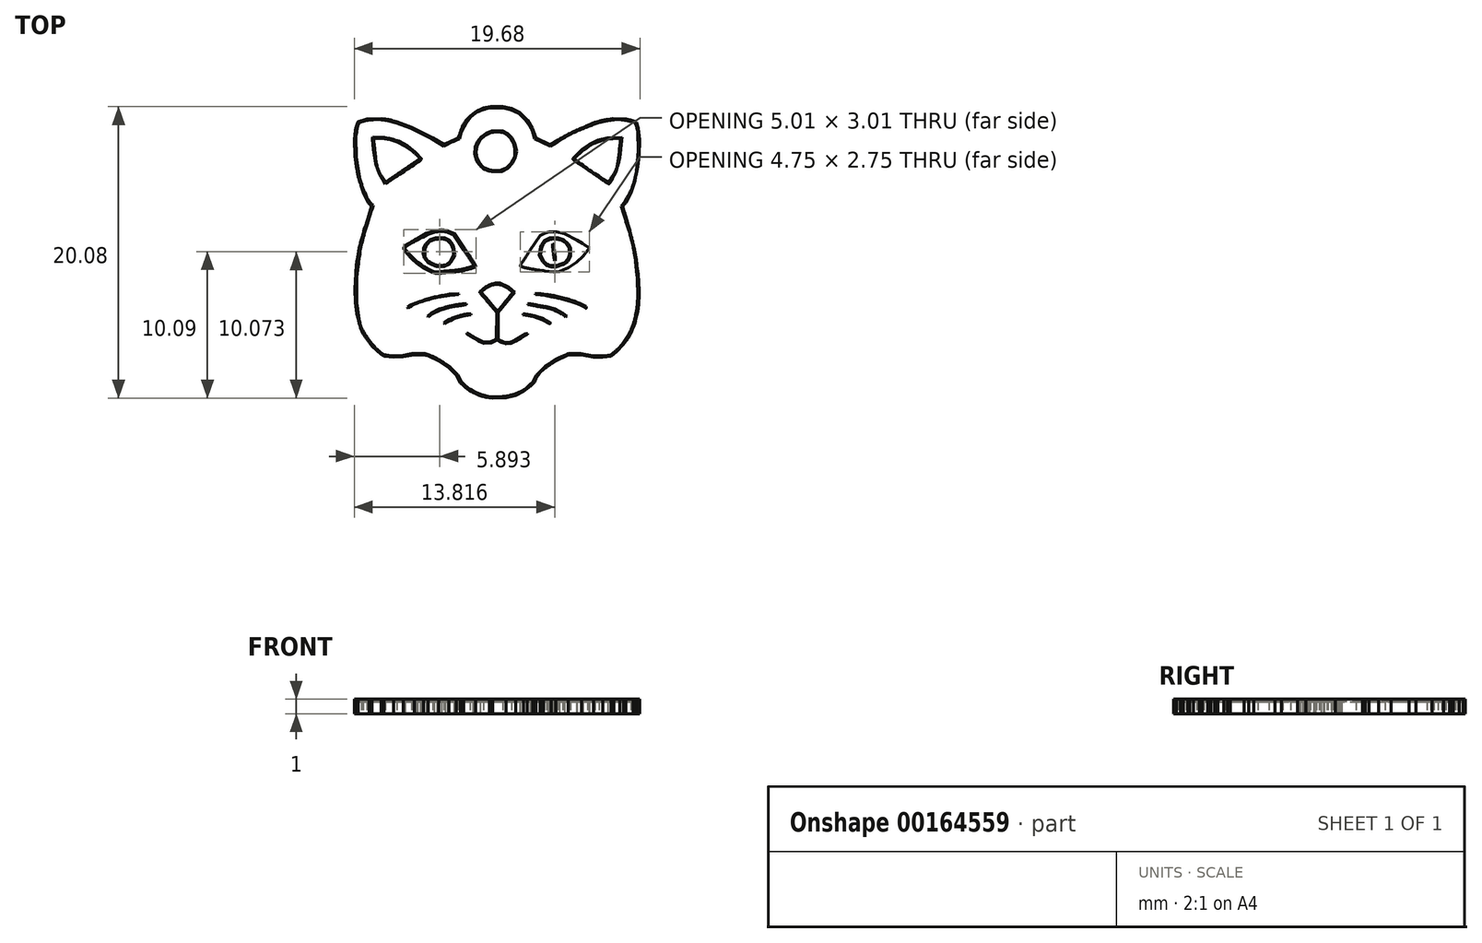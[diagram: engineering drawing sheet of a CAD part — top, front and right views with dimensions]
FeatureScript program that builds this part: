
annotation { "Feature Type Name" : "Feature", "Feature Type Description" : "" }
export const myFeature = defineFeature(function(context is Context, id is Id, definition is map)
    precondition{}
    {
        {
            var Q0;
            Q0=qCreatedBy(makeId("Top.planeOp"),FACE);
            var sketch = newSketch(context, id + "F0", { "sketchPlane" : qUnion([Q0])});
            skFitSpline(sketch, "E0", {"points": [v(-0.53, -10.01) * mm, v(-0.8, -9.97) * mm, v(-1.27, -9.84) * mm, v(-1.49, -9.74) * mm]});
            skFitSpline(sketch, "E1", {"points": [v(-1.49, -9.74) * mm, v(-1.72, -9.63) * mm, v(-2.05, -9.42) * mm, v(-2.3, -9.2) * mm]});
            skLineSegment(sketch, "E2", {"start": v(-2.3, -9.2) * mm, "end": v(-2.52, -9.01) * mm});
            skLineSegment(sketch, "E3", {"start": v(-2.52, -9.01) * mm, "end": v(-2.66, -8.74) * mm});
            skLineSegment(sketch, "E4", {"start": v(-2.66, -8.74) * mm, "end": v(-2.8, -8.47) * mm});
            skLineSegment(sketch, "E5", {"start": v(-2.8, -8.47) * mm, "end": v(-3.06, -8.22) * mm});
            skLineSegment(sketch, "E6", {"start": v(-3.06, -8.22) * mm, "end": v(-3.31, -7.96) * mm});
            skLineSegment(sketch, "E7", {"start": v(-3.31, -7.96) * mm, "end": v(-3.67, -7.72) * mm});
            skLineSegment(sketch, "E8", {"start": v(-3.67, -7.72) * mm, "end": v(-4.03, -7.49) * mm});
            skLineSegment(sketch, "E9", {"start": v(-4.03, -7.49) * mm, "end": v(-4.4, -7.3) * mm});
            skLineSegment(sketch, "E10", {"start": v(-4.4, -7.3) * mm, "end": v(-4.76, -7.13) * mm});
            skLineSegment(sketch, "E11", {"start": v(-4.76, -7.13) * mm, "end": v(-4.91, -7.1) * mm});
            skLineSegment(sketch, "E12", {"start": v(-4.91, -7.1) * mm, "end": v(-5.06, -7.06) * mm});
            skLineSegment(sketch, "E13", {"start": v(-5.06, -7.06) * mm, "end": v(-5.38, -7.06) * mm});
            skLineSegment(sketch, "E14", {"start": v(-5.38, -7.06) * mm, "end": v(-5.7, -7.06) * mm});
            skLineSegment(sketch, "E15", {"start": v(-5.7, -7.06) * mm, "end": v(-6.08, -7.12) * mm});
            skLineSegment(sketch, "E16", {"start": v(-6.08, -7.12) * mm, "end": v(-6.46, -7.2) * mm});
            skLineSegment(sketch, "E17", {"start": v(-6.46, -7.2) * mm, "end": v(-6.8, -7.21) * mm});
            skLineSegment(sketch, "E18", {"start": v(-6.8, -7.21) * mm, "end": v(-7.13, -7.23) * mm});
            skLineSegment(sketch, "E19", {"start": v(-7.13, -7.23) * mm, "end": v(-7.46, -7.2) * mm});
            skLineSegment(sketch, "E20", {"start": v(-7.46, -7.2) * mm, "end": v(-7.79, -7.15) * mm});
            skLineSegment(sketch, "E21", {"start": v(-7.79, -7.15) * mm, "end": v(-7.9, -7.1) * mm});
            skLineSegment(sketch, "E22", {"start": v(-7.9, -7.1) * mm, "end": v(-8, -7.05) * mm});
            skLineSegment(sketch, "E23", {"start": v(-8, -7.05) * mm, "end": v(-8.3, -6.76) * mm});
            skLineSegment(sketch, "E24", {"start": v(-8.3, -6.76) * mm, "end": v(-8.61, -6.48) * mm});
            skLineSegment(sketch, "E25", {"start": v(-8.61, -6.48) * mm, "end": v(-8.8, -6.22) * mm});
            skFitSpline(sketch, "E26", {"points": [v(-8.8, -6.22) * mm, v(-9.16, -5.74) * mm, v(-9.4, -5.2) * mm, v(-9.58, -4.56) * mm]});
            skLineSegment(sketch, "E27", {"start": v(-9.58, -4.56) * mm, "end": v(-9.66, -4.24) * mm});
            skLineSegment(sketch, "E28", {"start": v(-9.66, -4.24) * mm, "end": v(-9.71, -3.86) * mm});
            skLineSegment(sketch, "E29", {"start": v(-9.71, -3.86) * mm, "end": v(-9.76, -3.49) * mm});
            skLineSegment(sketch, "E30", {"start": v(-9.76, -3.49) * mm, "end": v(-9.78, -3) * mm});
            skLineSegment(sketch, "E31", {"start": v(-9.78, -3) * mm, "end": v(-9.8, -2.53) * mm});
            skLineSegment(sketch, "E32", {"start": v(-9.8, -2.53) * mm, "end": v(-9.76, -1.98) * mm});
            skFitSpline(sketch, "E33", {"points": [v(-9.76, -1.98) * mm, v(-9.67, -0.63) * mm, v(-9.37, 0.83) * mm, v(-8.85, 2.51) * mm]});
            skLineSegment(sketch, "E34", {"start": v(-8.85, 2.51) * mm, "end": v(-8.64, 3.2) * mm});
            skLineSegment(sketch, "E35", {"start": v(-8.64, 3.2) * mm, "end": v(-8.76, 3.3) * mm});
            skLineSegment(sketch, "E36", {"start": v(-8.76, 3.3) * mm, "end": v(-8.87, 3.42) * mm});
            skLineSegment(sketch, "E37", {"start": v(-8.87, 3.42) * mm, "end": v(-9.05, 3.77) * mm});
            skLineSegment(sketch, "E38", {"start": v(-9.05, 3.77) * mm, "end": v(-9.22, 4.13) * mm});
            skLineSegment(sketch, "E39", {"start": v(-9.22, 4.13) * mm, "end": v(-9.36, 4.54) * mm});
            skFitSpline(sketch, "E40", {"points": [v(-9.36, 4.54) * mm, v(-9.51, 5.02) * mm, v(-9.64, 5.58) * mm, v(-9.73, 6.17) * mm]});
            skLineSegment(sketch, "E41", {"start": v(-9.73, 6.17) * mm, "end": v(-9.8, 6.6) * mm});
            skLineSegment(sketch, "E42", {"start": v(-9.8, 6.6) * mm, "end": v(-9.82, 7.19) * mm});
            skLineSegment(sketch, "E43", {"start": v(-9.82, 7.19) * mm, "end": v(-9.84, 7.77) * mm});
            skLineSegment(sketch, "E44", {"start": v(-9.84, 7.77) * mm, "end": v(-9.8, 8.1) * mm});
            skLineSegment(sketch, "E45", {"start": v(-9.8, 8.1) * mm, "end": v(-9.76, 8.43) * mm});
            skLineSegment(sketch, "E46", {"start": v(-9.76, 8.43) * mm, "end": v(-9.7, 8.68) * mm});
            skFitSpline(sketch, "E47", {"points": [v(-9.7, 8.68) * mm, v(-9.65, 8.82) * mm, v(-9.61, 8.95) * mm, v(-9.6, 8.97) * mm]});
            skLineSegment(sketch, "E48", {"start": v(-9.6, 8.97) * mm, "end": v(-9.58, 9) * mm});
            skLineSegment(sketch, "E49", {"start": v(-9.58, 9) * mm, "end": v(-9.28, 9.1) * mm});
            skLineSegment(sketch, "E50", {"start": v(-9.28, 9.1) * mm, "end": v(-8.98, 9.19) * mm});
            skLineSegment(sketch, "E51", {"start": v(-8.98, 9.19) * mm, "end": v(-8.48, 9.2) * mm});
            skLineSegment(sketch, "E52", {"start": v(-8.48, 9.2) * mm, "end": v(-7.97, 9.22) * mm});
            skLineSegment(sketch, "E53", {"start": v(-7.97, 9.22) * mm, "end": v(-7.7, 9.18) * mm});
            skFitSpline(sketch, "E54", {"points": [v(-7.7, 9.18) * mm, v(-7.54, 9.16) * mm, v(-7.3, 9.11) * mm, v(-7.16, 9.08) * mm]});
            skLineSegment(sketch, "E55", {"start": v(-7.16, 9.08) * mm, "end": v(-6.91, 9.01) * mm});
            skLineSegment(sketch, "E56", {"start": v(-6.91, 9.01) * mm, "end": v(-6.4, 8.81) * mm});
            skLineSegment(sketch, "E57", {"start": v(-6.4, 8.81) * mm, "end": v(-5.9, 8.6) * mm});
            skLineSegment(sketch, "E58", {"start": v(-5.9, 8.6) * mm, "end": v(-5.16, 8.25) * mm});
            skLineSegment(sketch, "E59", {"start": v(-5.16, 8.25) * mm, "end": v(-4.43, 7.89) * mm});
            skLineSegment(sketch, "E60", {"start": v(-4.43, 7.89) * mm, "end": v(-4.05, 7.66) * mm});
            skLineSegment(sketch, "E61", {"start": v(-4.05, 7.66) * mm, "end": v(-3.67, 7.43) * mm});
            skLineSegment(sketch, "E62", {"start": v(-3.67, 7.43) * mm, "end": v(-3.44, 7.53) * mm});
            skFitSpline(sketch, "E63", {"points": [v(-3.44, 7.53) * mm, v(-3.3, 7.6) * mm, v(-3.08, 7.7) * mm, v(-2.94, 7.77) * mm]});
            skLineSegment(sketch, "E64", {"start": v(-2.94, 7.77) * mm, "end": v(-2.68, 7.9) * mm});
            skLineSegment(sketch, "E65", {"start": v(-2.68, 7.9) * mm, "end": v(-2.57, 8.18) * mm});
            skFitSpline(sketch, "E66", {"points": [v(-2.57, 8.18) * mm, v(-2.38, 8.7) * mm, v(-2.16, 9.07) * mm, v(-1.85, 9.37) * mm]});
            skLineSegment(sketch, "E67", {"start": v(-1.85, 9.37) * mm, "end": v(-1.68, 9.55) * mm});
            skLineSegment(sketch, "E68", {"start": v(-1.68, 9.55) * mm, "end": v(-1.5, 9.66) * mm});
            skFitSpline(sketch, "E69", {"points": [v(-1.5, 9.66) * mm, v(-1.42, 9.72) * mm, v(-1.25, 9.8) * mm, v(-1.14, 9.85) * mm]});
            skLineSegment(sketch, "E70", {"start": v(-1.14, 9.85) * mm, "end": v(-0.95, 9.94) * mm});
            skLineSegment(sketch, "E71", {"start": v(-0.95, 9.94) * mm, "end": v(-0.69, 9.99) * mm});
            skLineSegment(sketch, "E72", {"start": v(-0.69, 9.99) * mm, "end": v(-0.43, 10.04) * mm});
            skLineSegment(sketch, "E73", {"start": v(-0.43, 10.04) * mm, "end": v(-0.03, 10.04) * mm});
            skLineSegment(sketch, "E74", {"start": v(-0.03, 10.04) * mm, "end": v(0.38, 10.04) * mm});
            skLineSegment(sketch, "E75", {"start": v(0.38, 10.04) * mm, "end": v(0.7, 9.98) * mm});
            skLineSegment(sketch, "E76", {"start": v(0.7, 9.98) * mm, "end": v(1, 9.91) * mm});
            skLineSegment(sketch, "E77", {"start": v(1, 9.91) * mm, "end": v(1.29, 9.77) * mm});
            skLineSegment(sketch, "E78", {"start": v(1.29, 9.77) * mm, "end": v(1.57, 9.64) * mm});
            skLineSegment(sketch, "E79", {"start": v(1.57, 9.64) * mm, "end": v(1.84, 9.36) * mm});
            skLineSegment(sketch, "E80", {"start": v(1.84, 9.36) * mm, "end": v(2.1, 9.1) * mm});
            skLineSegment(sketch, "E81", {"start": v(2.1, 9.1) * mm, "end": v(2.27, 8.83) * mm});
            skLineSegment(sketch, "E82", {"start": v(2.27, 8.83) * mm, "end": v(2.42, 8.56) * mm});
            skLineSegment(sketch, "E83", {"start": v(2.42, 8.56) * mm, "end": v(2.55, 8.22) * mm});
            skLineSegment(sketch, "E84", {"start": v(2.55, 8.22) * mm, "end": v(2.68, 7.88) * mm});
            skLineSegment(sketch, "E85", {"start": v(2.68, 7.88) * mm, "end": v(3.17, 7.65) * mm});
            skLineSegment(sketch, "E86", {"start": v(3.17, 7.65) * mm, "end": v(3.66, 7.42) * mm});
            skLineSegment(sketch, "E87", {"start": v(3.66, 7.42) * mm, "end": v(4.08, 7.67) * mm});
            skFitSpline(sketch, "E88", {"points": [v(4.08, 7.67) * mm, v(4.62, 8) * mm, v(5.55, 8.45) * mm, v(6.23, 8.73) * mm]});
            skLineSegment(sketch, "E89", {"start": v(6.23, 8.73) * mm, "end": v(6.76, 8.95) * mm});
            skLineSegment(sketch, "E90", {"start": v(6.76, 8.95) * mm, "end": v(7.04, 9.03) * mm});
            skFitSpline(sketch, "E91", {"points": [v(7.04, 9.03) * mm, v(7.2, 9.08) * mm, v(7.47, 9.14) * mm, v(7.65, 9.17) * mm]});
            skLineSegment(sketch, "E92", {"start": v(7.65, 9.17) * mm, "end": v(7.98, 9.22) * mm});
            skLineSegment(sketch, "E93", {"start": v(7.98, 9.22) * mm, "end": v(8.45, 9.2) * mm});
            skLineSegment(sketch, "E94", {"start": v(8.45, 9.2) * mm, "end": v(8.92, 9.19) * mm});
            skLineSegment(sketch, "E95", {"start": v(8.92, 9.19) * mm, "end": v(9.17, 9.12) * mm});
            skFitSpline(sketch, "E96", {"points": [v(9.17, 9.12) * mm, v(9.32, 9.08) * mm, v(9.47, 9.03) * mm, v(9.52, 9) * mm]});
            skLineSegment(sketch, "E97", {"start": v(9.52, 9) * mm, "end": v(9.6, 8.96) * mm});
            skLineSegment(sketch, "E98", {"start": v(9.6, 8.96) * mm, "end": v(9.67, 8.76) * mm});
            skLineSegment(sketch, "E99", {"start": v(9.67, 8.76) * mm, "end": v(9.73, 8.56) * mm});
            skLineSegment(sketch, "E100", {"start": v(9.73, 8.56) * mm, "end": v(9.78, 8.17) * mm});
            skLineSegment(sketch, "E101", {"start": v(9.78, 8.17) * mm, "end": v(9.84, 7.77) * mm});
            skLineSegment(sketch, "E102", {"start": v(9.84, 7.77) * mm, "end": v(9.82, 7.2) * mm});
            skLineSegment(sketch, "E103", {"start": v(9.82, 7.2) * mm, "end": v(9.8, 6.64) * mm});
            skLineSegment(sketch, "E104", {"start": v(9.8, 6.64) * mm, "end": v(9.73, 6.17) * mm});
            skFitSpline(sketch, "E105", {"points": [v(9.73, 6.17) * mm, v(9.7, 5.92) * mm, v(9.62, 5.54) * mm, v(9.58, 5.33) * mm]});
            skLineSegment(sketch, "E106", {"start": v(9.58, 5.33) * mm, "end": v(9.5, 4.95) * mm});
            skLineSegment(sketch, "E107", {"start": v(9.5, 4.95) * mm, "end": v(9.35, 4.5) * mm});
            skLineSegment(sketch, "E108", {"start": v(9.35, 4.5) * mm, "end": v(9.2, 4.07) * mm});
            skLineSegment(sketch, "E109", {"start": v(9.2, 4.07) * mm, "end": v(9.03, 3.74) * mm});
            skLineSegment(sketch, "E110", {"start": v(9.03, 3.74) * mm, "end": v(8.87, 3.42) * mm});
            skLineSegment(sketch, "E111", {"start": v(8.87, 3.42) * mm, "end": v(8.75, 3.3) * mm});
            skLineSegment(sketch, "E112", {"start": v(8.75, 3.3) * mm, "end": v(8.63, 3.17) * mm});
            skLineSegment(sketch, "E113", {"start": v(8.63, 3.17) * mm, "end": v(8.7, 2.98) * mm});
            skFitSpline(sketch, "E114", {"points": [v(8.7, 2.98) * mm, v(8.81, 2.66) * mm, v(9.12, 1.6) * mm, v(9.24, 1.1) * mm]});
            skFitSpline(sketch, "E115", {"points": [v(9.24, 1.1) * mm, v(9.42, 0.4) * mm, v(9.55, -0.28) * mm, v(9.64, -0.92) * mm]});
            skLineSegment(sketch, "E116", {"start": v(9.64, -0.92) * mm, "end": v(9.73, -1.5) * mm});
            skLineSegment(sketch, "E117", {"start": v(9.73, -1.5) * mm, "end": v(9.76, -2.06) * mm});
            skLineSegment(sketch, "E118", {"start": v(9.76, -2.06) * mm, "end": v(9.8, -2.63) * mm});
            skLineSegment(sketch, "E119", {"start": v(9.8, -2.63) * mm, "end": v(9.78, -3.06) * mm});
            skFitSpline(sketch, "E120", {"points": [v(9.78, -3.06) * mm, v(9.75, -3.6) * mm, v(9.69, -4.09) * mm, v(9.58, -4.53) * mm]});
            skLineSegment(sketch, "E121", {"start": v(9.58, -4.53) * mm, "end": v(9.5, -4.88) * mm});
            skLineSegment(sketch, "E122", {"start": v(9.5, -4.88) * mm, "end": v(9.38, -5.18) * mm});
            skFitSpline(sketch, "E123", {"points": [v(9.38, -5.18) * mm, v(9.23, -5.54) * mm, v(9.08, -5.83) * mm, v(8.87, -6.13) * mm]});
            skLineSegment(sketch, "E124", {"start": v(8.87, -6.13) * mm, "end": v(8.72, -6.34) * mm});
            skLineSegment(sketch, "E125", {"start": v(8.72, -6.34) * mm, "end": v(8.47, -6.6) * mm});
            skFitSpline(sketch, "E126", {"points": [v(8.47, -6.6) * mm, v(8.33, -6.75) * mm, v(8.14, -6.93) * mm, v(8.04, -7) * mm]});
            skLineSegment(sketch, "E127", {"start": v(8.04, -7) * mm, "end": v(7.85, -7.15) * mm});
            skLineSegment(sketch, "E128", {"start": v(7.85, -7.15) * mm, "end": v(7.57, -7.19) * mm});
            skLineSegment(sketch, "E129", {"start": v(7.57, -7.19) * mm, "end": v(7.3, -7.22) * mm});
            skLineSegment(sketch, "E130", {"start": v(7.3, -7.22) * mm, "end": v(6.98, -7.22) * mm});
            skLineSegment(sketch, "E131", {"start": v(6.98, -7.22) * mm, "end": v(6.66, -7.22) * mm});
            skLineSegment(sketch, "E132", {"start": v(6.66, -7.22) * mm, "end": v(6.24, -7.15) * mm});
            skLineSegment(sketch, "E133", {"start": v(6.24, -7.15) * mm, "end": v(5.83, -7.08) * mm});
            skLineSegment(sketch, "E134", {"start": v(5.83, -7.08) * mm, "end": v(5.36, -7.08) * mm});
            skLineSegment(sketch, "E135", {"start": v(5.36, -7.08) * mm, "end": v(4.9, -7.08) * mm});
            skLineSegment(sketch, "E136", {"start": v(4.9, -7.08) * mm, "end": v(4.47, -7.28) * mm});
            skLineSegment(sketch, "E137", {"start": v(4.47, -7.28) * mm, "end": v(4.04, -7.49) * mm});
            skLineSegment(sketch, "E138", {"start": v(4.04, -7.49) * mm, "end": v(3.72, -7.7) * mm});
            skFitSpline(sketch, "E139", {"points": [v(3.72, -7.7) * mm, v(3.55, -7.81) * mm, v(3.3, -8) * mm, v(3.19, -8.1) * mm]});
            skLineSegment(sketch, "E140", {"start": v(3.19, -8.1) * mm, "end": v(2.97, -8.28) * mm});
            skLineSegment(sketch, "E141", {"start": v(2.97, -8.28) * mm, "end": v(2.82, -8.48) * mm});
            skLineSegment(sketch, "E142", {"start": v(2.82, -8.48) * mm, "end": v(2.68, -8.68) * mm});
            skLineSegment(sketch, "E143", {"start": v(2.68, -8.68) * mm, "end": v(2.62, -8.82) * mm});
            skLineSegment(sketch, "E144", {"start": v(2.62, -8.82) * mm, "end": v(2.57, -8.95) * mm});
            skLineSegment(sketch, "E145", {"start": v(2.57, -8.95) * mm, "end": v(2.46, -9.07) * mm});
            skFitSpline(sketch, "E146", {"points": [v(2.46, -9.07) * mm, v(2.4, -9.13) * mm, v(2.22, -9.28) * mm, v(2.08, -9.38) * mm]});
            skLineSegment(sketch, "E147", {"start": v(2.08, -9.38) * mm, "end": v(1.82, -9.58) * mm});
            skLineSegment(sketch, "E148", {"start": v(1.82, -9.58) * mm, "end": v(1.55, -9.71) * mm});
            skLineSegment(sketch, "E149", {"start": v(1.55, -9.71) * mm, "end": v(1.27, -9.85) * mm});
            skLineSegment(sketch, "E150", {"start": v(1.27, -9.85) * mm, "end": v(0.94, -9.93) * mm});
            skLineSegment(sketch, "E151", {"start": v(0.94, -9.93) * mm, "end": v(0.62, -10.02) * mm});
            skLineSegment(sketch, "E152", {"start": v(0.62, -10.02) * mm, "end": v(0.15, -10.03) * mm});
            skLineSegment(sketch, "E153", {"start": v(0.15, -10.03) * mm, "end": v(-0.31, -10.04) * mm});
            skLineSegment(sketch, "E154", {"start": v(-0.31, -10.04) * mm, "end": v(-0.53, -10.01) * mm});
            skLineSegment(sketch, "E155", {"start": v(-0.53, -10.01) * mm, "end": v(-0.53, -10.01) * mm});
            skFitSpline(sketch, "E156", {"points": [v(0.48, -9.93) * mm, v(0.6, -9.92) * mm, v(0.8, -9.88) * mm, v(0.95, -9.84) * mm]});
            skLineSegment(sketch, "E157", {"start": v(0.95, -9.84) * mm, "end": v(1.21, -9.77) * mm});
            skLineSegment(sketch, "E158", {"start": v(1.21, -9.77) * mm, "end": v(1.45, -9.67) * mm});
            skFitSpline(sketch, "E159", {"points": [v(1.45, -9.67) * mm, v(1.74, -9.53) * mm, v(2.02, -9.34) * mm, v(2.27, -9.11) * mm]});
            skLineSegment(sketch, "E160", {"start": v(2.27, -9.11) * mm, "end": v(2.46, -8.94) * mm});
            skLineSegment(sketch, "E161", {"start": v(2.46, -8.94) * mm, "end": v(2.58, -8.7) * mm});
            skLineSegment(sketch, "E162", {"start": v(2.58, -8.7) * mm, "end": v(2.7, -8.47) * mm});
            skLineSegment(sketch, "E163", {"start": v(2.7, -8.47) * mm, "end": v(3, -8.17) * mm});
            skLineSegment(sketch, "E164", {"start": v(3, -8.17) * mm, "end": v(3.3, -7.87) * mm});
            skLineSegment(sketch, "E165", {"start": v(3.3, -7.87) * mm, "end": v(3.62, -7.66) * mm});
            skFitSpline(sketch, "E166", {"points": [v(3.62, -7.66) * mm, v(3.93, -7.45) * mm, v(4.43, -7.18) * mm, v(4.76, -7.05) * mm]});
            skLineSegment(sketch, "E167", {"start": v(4.76, -7.05) * mm, "end": v(4.93, -6.98) * mm});
            skLineSegment(sketch, "E168", {"start": v(4.93, -6.98) * mm, "end": v(5.35, -6.98) * mm});
            skLineSegment(sketch, "E169", {"start": v(5.35, -6.98) * mm, "end": v(5.76, -6.99) * mm});
            skLineSegment(sketch, "E170", {"start": v(5.76, -6.99) * mm, "end": v(6.18, -7.06) * mm});
            skLineSegment(sketch, "E171", {"start": v(6.18, -7.06) * mm, "end": v(6.6, -7.13) * mm});
            skLineSegment(sketch, "E172", {"start": v(6.6, -7.13) * mm, "end": v(6.99, -7.13) * mm});
            skLineSegment(sketch, "E173", {"start": v(6.99, -7.13) * mm, "end": v(7.39, -7.13) * mm});
            skLineSegment(sketch, "E174", {"start": v(7.39, -7.13) * mm, "end": v(7.6, -7.1) * mm});
            skLineSegment(sketch, "E175", {"start": v(7.6, -7.1) * mm, "end": v(7.81, -7.06) * mm});
            skLineSegment(sketch, "E176", {"start": v(7.81, -7.06) * mm, "end": v(7.95, -6.97) * mm});
            skFitSpline(sketch, "E177", {"points": [v(7.95, -6.97) * mm, v(8.02, -6.92) * mm, v(8.2, -6.76) * mm, v(8.35, -6.6) * mm]});
            skLineSegment(sketch, "E178", {"start": v(8.35, -6.6) * mm, "end": v(8.62, -6.34) * mm});
            skLineSegment(sketch, "E179", {"start": v(8.62, -6.34) * mm, "end": v(8.84, -6) * mm});
            skLineSegment(sketch, "E180", {"start": v(8.84, -6) * mm, "end": v(9.06, -5.68) * mm});
            skLineSegment(sketch, "E181", {"start": v(9.06, -5.68) * mm, "end": v(9.18, -5.43) * mm});
            skFitSpline(sketch, "E182", {"points": [v(9.18, -5.43) * mm, v(9.33, -5.1) * mm, v(9.48, -4.62) * mm, v(9.56, -4.21) * mm]});
            skLineSegment(sketch, "E183", {"start": v(9.56, -4.21) * mm, "end": v(9.63, -3.89) * mm});
            skLineSegment(sketch, "E184", {"start": v(9.63, -3.89) * mm, "end": v(9.67, -3.47) * mm});
            skLineSegment(sketch, "E185", {"start": v(9.67, -3.47) * mm, "end": v(9.7, -3.06) * mm});
            skLineSegment(sketch, "E186", {"start": v(9.7, -3.06) * mm, "end": v(9.69, -2.4) * mm});
            skLineSegment(sketch, "E187", {"start": v(9.69, -2.4) * mm, "end": v(9.67, -1.76) * mm});
            skLineSegment(sketch, "E188", {"start": v(9.67, -1.76) * mm, "end": v(9.61, -1.33) * mm});
            skFitSpline(sketch, "E189", {"points": [v(9.61, -1.33) * mm, v(9.47, -0.15) * mm, v(9.17, 1.18) * mm, v(8.7, 2.67) * mm]});
            skLineSegment(sketch, "E190", {"start": v(8.7, 2.67) * mm, "end": v(8.55, 3.2) * mm});
            skLineSegment(sketch, "E191", {"start": v(8.55, 3.2) * mm, "end": v(8.67, 3.34) * mm});
            skLineSegment(sketch, "E192", {"start": v(8.67, 3.34) * mm, "end": v(8.8, 3.48) * mm});
            skLineSegment(sketch, "E193", {"start": v(8.8, 3.48) * mm, "end": v(8.95, 3.77) * mm});
            skFitSpline(sketch, "E194", {"points": [v(8.95, 3.77) * mm, v(9.3, 4.46) * mm, v(9.59, 5.53) * mm, v(9.7, 6.63) * mm]});
            skLineSegment(sketch, "E195", {"start": v(9.7, 6.63) * mm, "end": v(9.74, 7.03) * mm});
            skLineSegment(sketch, "E196", {"start": v(9.74, 7.03) * mm, "end": v(9.72, 7.65) * mm});
            skLineSegment(sketch, "E197", {"start": v(9.72, 7.65) * mm, "end": v(9.7, 8.27) * mm});
            skLineSegment(sketch, "E198", {"start": v(9.7, 8.27) * mm, "end": v(9.65, 8.49) * mm});
            skFitSpline(sketch, "E199", {"points": [v(9.65, 8.49) * mm, v(9.62, 8.61) * mm, v(9.58, 8.76) * mm, v(9.55, 8.82) * mm]});
            skLineSegment(sketch, "E200", {"start": v(9.55, 8.82) * mm, "end": v(9.5, 8.94) * mm});
            skLineSegment(sketch, "E201", {"start": v(9.5, 8.94) * mm, "end": v(9.24, 9) * mm});
            skLineSegment(sketch, "E202", {"start": v(9.24, 9) * mm, "end": v(8.98, 9.08) * mm});
            skLineSegment(sketch, "E203", {"start": v(8.98, 9.08) * mm, "end": v(8.66, 9.11) * mm});
            skLineSegment(sketch, "E204", {"start": v(8.66, 9.11) * mm, "end": v(8.33, 9.15) * mm});
            skLineSegment(sketch, "E205", {"start": v(8.33, 9.15) * mm, "end": v(7.96, 9.11) * mm});
            skLineSegment(sketch, "E206", {"start": v(7.96, 9.11) * mm, "end": v(7.59, 9.08) * mm});
            skLineSegment(sketch, "E207", {"start": v(7.59, 9.08) * mm, "end": v(7.29, 9) * mm});
            skLineSegment(sketch, "E208", {"start": v(7.29, 9) * mm, "end": v(6.99, 8.94) * mm});
            skLineSegment(sketch, "E209", {"start": v(6.99, 8.94) * mm, "end": v(6.62, 8.8) * mm});
            skFitSpline(sketch, "E210", {"points": [v(6.62, 8.8) * mm, v(5.75, 8.46) * mm, v(4.82, 8) * mm, v(4.06, 7.55) * mm]});
            skLineSegment(sketch, "E211", {"start": v(4.06, 7.55) * mm, "end": v(3.67, 7.32) * mm});
            skLineSegment(sketch, "E212", {"start": v(3.67, 7.32) * mm, "end": v(3.13, 7.57) * mm});
            skLineSegment(sketch, "E213", {"start": v(3.13, 7.57) * mm, "end": v(2.6, 7.82) * mm});
            skLineSegment(sketch, "E214", {"start": v(2.6, 7.82) * mm, "end": v(2.52, 8.04) * mm});
            skFitSpline(sketch, "E215", {"points": [v(2.52, 8.04) * mm, v(2.41, 8.38) * mm, v(2.28, 8.66) * mm, v(2.11, 8.91) * mm]});
            skLineSegment(sketch, "E216", {"start": v(2.11, 8.91) * mm, "end": v(1.96, 9.14) * mm});
            skLineSegment(sketch, "E217", {"start": v(1.96, 9.14) * mm, "end": v(1.73, 9.36) * mm});
            skLineSegment(sketch, "E218", {"start": v(1.73, 9.36) * mm, "end": v(1.5, 9.57) * mm});
            skLineSegment(sketch, "E219", {"start": v(1.5, 9.57) * mm, "end": v(1.22, 9.7) * mm});
            skLineSegment(sketch, "E220", {"start": v(1.22, 9.7) * mm, "end": v(0.95, 9.84) * mm});
            skLineSegment(sketch, "E221", {"start": v(0.95, 9.84) * mm, "end": v(0.68, 9.9) * mm});
            skLineSegment(sketch, "E222", {"start": v(0.68, 9.9) * mm, "end": v(0.42, 9.95) * mm});
            skLineSegment(sketch, "E223", {"start": v(0.42, 9.95) * mm, "end": v(-0.05, 9.95) * mm});
            skLineSegment(sketch, "E224", {"start": v(-0.05, 9.95) * mm, "end": v(-0.51, 9.95) * mm});
            skLineSegment(sketch, "E225", {"start": v(-0.51, 9.95) * mm, "end": v(-0.78, 9.88) * mm});
            skFitSpline(sketch, "E226", {"points": [v(-0.78, 9.88) * mm, v(-0.92, 9.84) * mm, v(-1.12, 9.77) * mm, v(-1.2, 9.73) * mm]});
            skLineSegment(sketch, "E227", {"start": v(-1.2, 9.73) * mm, "end": v(-1.38, 9.65) * mm});
            skLineSegment(sketch, "E228", {"start": v(-1.38, 9.65) * mm, "end": v(-1.59, 9.5) * mm});
            skLineSegment(sketch, "E229", {"start": v(-1.59, 9.5) * mm, "end": v(-1.8, 9.34) * mm});
            skLineSegment(sketch, "E230", {"start": v(-1.8, 9.34) * mm, "end": v(-1.96, 9.13) * mm});
            skLineSegment(sketch, "E231", {"start": v(-1.96, 9.13) * mm, "end": v(-2.13, 8.93) * mm});
            skLineSegment(sketch, "E232", {"start": v(-2.13, 8.93) * mm, "end": v(-2.29, 8.6) * mm});
            skLineSegment(sketch, "E233", {"start": v(-2.29, 8.6) * mm, "end": v(-2.45, 8.29) * mm});
            skLineSegment(sketch, "E234", {"start": v(-2.45, 8.29) * mm, "end": v(-2.53, 8.05) * mm});
            skLineSegment(sketch, "E235", {"start": v(-2.53, 8.05) * mm, "end": v(-2.6, 7.82) * mm});
            skLineSegment(sketch, "E236", {"start": v(-2.6, 7.82) * mm, "end": v(-2.82, 7.72) * mm});
            skFitSpline(sketch, "E237", {"points": [v(-2.82, 7.72) * mm, v(-2.94, 7.67) * mm, v(-3.18, 7.56) * mm, v(-3.36, 7.48) * mm]});
            skLineSegment(sketch, "E238", {"start": v(-3.36, 7.48) * mm, "end": v(-3.67, 7.33) * mm});
            skLineSegment(sketch, "E239", {"start": v(-3.67, 7.33) * mm, "end": v(-4.09, 7.58) * mm});
            skLineSegment(sketch, "E240", {"start": v(-4.09, 7.58) * mm, "end": v(-4.5, 7.82) * mm});
            skLineSegment(sketch, "E241", {"start": v(-4.5, 7.82) * mm, "end": v(-5.23, 8.18) * mm});
            skLineSegment(sketch, "E242", {"start": v(-5.23, 8.18) * mm, "end": v(-5.96, 8.54) * mm});
            skLineSegment(sketch, "E243", {"start": v(-5.96, 8.54) * mm, "end": v(-6.43, 8.73) * mm});
            skLineSegment(sketch, "E244", {"start": v(-6.43, 8.73) * mm, "end": v(-6.9, 8.92) * mm});
            skLineSegment(sketch, "E245", {"start": v(-6.9, 8.92) * mm, "end": v(-7.21, 9) * mm});
            skLineSegment(sketch, "E246", {"start": v(-7.21, 9) * mm, "end": v(-7.52, 9.07) * mm});
            skLineSegment(sketch, "E247", {"start": v(-7.52, 9.07) * mm, "end": v(-7.87, 9.11) * mm});
            skLineSegment(sketch, "E248", {"start": v(-7.87, 9.11) * mm, "end": v(-8.22, 9.15) * mm});
            skLineSegment(sketch, "E249", {"start": v(-8.22, 9.15) * mm, "end": v(-8.52, 9.13) * mm});
            skFitSpline(sketch, "E250", {"points": [v(-8.52, 9.13) * mm, v(-8.84, 9.11) * mm, v(-9.03, 9.08) * mm, v(-9.34, 9) * mm]});
            skLineSegment(sketch, "E251", {"start": v(-9.34, 9) * mm, "end": v(-9.53, 8.94) * mm});
            skLineSegment(sketch, "E252", {"start": v(-9.53, 8.94) * mm, "end": v(-9.58, 8.78) * mm});
            skFitSpline(sketch, "E253", {"points": [v(-9.58, 8.78) * mm, v(-9.6, 8.7) * mm, v(-9.65, 8.49) * mm, v(-9.68, 8.32) * mm]});
            skLineSegment(sketch, "E254", {"start": v(-9.68, 8.32) * mm, "end": v(-9.73, 8) * mm});
            skLineSegment(sketch, "E255", {"start": v(-9.73, 8) * mm, "end": v(-9.72, 7.25) * mm});
            skLineSegment(sketch, "E256", {"start": v(-9.72, 7.25) * mm, "end": v(-9.7, 6.5) * mm});
            skLineSegment(sketch, "E257", {"start": v(-9.7, 6.5) * mm, "end": v(-9.65, 6.16) * mm});
            skFitSpline(sketch, "E258", {"points": [v(-9.65, 6.16) * mm, v(-9.53, 5.4) * mm, v(-9.34, 4.68) * mm, v(-9.12, 4.13) * mm]});
            skLineSegment(sketch, "E259", {"start": v(-9.12, 4.13) * mm, "end": v(-8.97, 3.77) * mm});
            skLineSegment(sketch, "E260", {"start": v(-8.97, 3.77) * mm, "end": v(-8.82, 3.54) * mm});
            skLineSegment(sketch, "E261", {"start": v(-8.82, 3.54) * mm, "end": v(-8.66, 3.3) * mm});
            skLineSegment(sketch, "E262", {"start": v(-8.66, 3.3) * mm, "end": v(-8.6, 3.27) * mm});
            skLineSegment(sketch, "E263", {"start": v(-8.6, 3.27) * mm, "end": v(-8.54, 3.24) * mm});
            skLineSegment(sketch, "E264", {"start": v(-8.54, 3.24) * mm, "end": v(-8.6, 3.03) * mm});
            skFitSpline(sketch, "E265", {"points": [v(-8.6, 3.03) * mm, v(-9.16, 1.24) * mm, v(-9.42, 0.12) * mm, v(-9.6, -1.2) * mm]});
            skLineSegment(sketch, "E266", {"start": v(-9.6, -1.2) * mm, "end": v(-9.67, -1.73) * mm});
            skLineSegment(sketch, "E267", {"start": v(-9.67, -1.73) * mm, "end": v(-9.68, -2.64) * mm});
            skLineSegment(sketch, "E268", {"start": v(-9.68, -2.64) * mm, "end": v(-9.68, -3.55) * mm});
            skLineSegment(sketch, "E269", {"start": v(-9.68, -3.55) * mm, "end": v(-9.62, -3.9) * mm});
            skFitSpline(sketch, "E270", {"points": [v(-9.62, -3.9) * mm, v(-9.48, -4.8) * mm, v(-9.25, -5.4) * mm, v(-8.83, -6.01) * mm]});
            skLineSegment(sketch, "E271", {"start": v(-8.83, -6.01) * mm, "end": v(-8.64, -6.31) * mm});
            skLineSegment(sketch, "E272", {"start": v(-8.64, -6.31) * mm, "end": v(-8.44, -6.5) * mm});
            skFitSpline(sketch, "E273", {"points": [v(-8.44, -6.5) * mm, v(-8.34, -6.62) * mm, v(-8.16, -6.79) * mm, v(-8.05, -6.88) * mm]});
            skLineSegment(sketch, "E274", {"start": v(-8.05, -6.88) * mm, "end": v(-7.84, -7.05) * mm});
            skLineSegment(sketch, "E275", {"start": v(-7.84, -7.05) * mm, "end": v(-7.59, -7.09) * mm});
            skLineSegment(sketch, "E276", {"start": v(-7.59, -7.09) * mm, "end": v(-7.33, -7.12) * mm});
            skLineSegment(sketch, "E277", {"start": v(-7.33, -7.12) * mm, "end": v(-6.97, -7.12) * mm});
            skLineSegment(sketch, "E278", {"start": v(-6.97, -7.12) * mm, "end": v(-6.61, -7.12) * mm});
            skLineSegment(sketch, "E279", {"start": v(-6.61, -7.12) * mm, "end": v(-6.24, -7.06) * mm});
            skLineSegment(sketch, "E280", {"start": v(-6.24, -7.06) * mm, "end": v(-5.86, -6.99) * mm});
            skLineSegment(sketch, "E281", {"start": v(-5.86, -6.99) * mm, "end": v(-5.42, -6.97) * mm});
            skLineSegment(sketch, "E282", {"start": v(-5.42, -6.97) * mm, "end": v(-4.98, -6.96) * mm});
            skLineSegment(sketch, "E283", {"start": v(-4.98, -6.96) * mm, "end": v(-4.69, -7.08) * mm});
            skFitSpline(sketch, "E284", {"points": [v(-4.69, -7.08) * mm, v(-4.3, -7.23) * mm, v(-3.98, -7.42) * mm, v(-3.57, -7.7) * mm]});
            skLineSegment(sketch, "E285", {"start": v(-3.57, -7.7) * mm, "end": v(-3.23, -7.92) * mm});
            skLineSegment(sketch, "E286", {"start": v(-3.23, -7.92) * mm, "end": v(-2.97, -8.18) * mm});
            skLineSegment(sketch, "E287", {"start": v(-2.97, -8.18) * mm, "end": v(-2.72, -8.43) * mm});
            skLineSegment(sketch, "E288", {"start": v(-2.72, -8.43) * mm, "end": v(-2.6, -8.68) * mm});
            skLineSegment(sketch, "E289", {"start": v(-2.6, -8.68) * mm, "end": v(-2.48, -8.92) * mm});
            skLineSegment(sketch, "E290", {"start": v(-2.48, -8.92) * mm, "end": v(-2.28, -9.1) * mm});
            skFitSpline(sketch, "E291", {"points": [v(-2.28, -9.1) * mm, v(-2.16, -9.2) * mm, v(-1.96, -9.36) * mm, v(-1.83, -9.45) * mm]});
            skLineSegment(sketch, "E292", {"start": v(-1.83, -9.45) * mm, "end": v(-1.58, -9.62) * mm});
            skLineSegment(sketch, "E293", {"start": v(-1.58, -9.62) * mm, "end": v(-1.32, -9.71) * mm});
            skFitSpline(sketch, "E294", {"points": [v(-1.32, -9.71) * mm, v(-1.18, -9.77) * mm, v(-0.96, -9.84) * mm, v(-0.84, -9.87) * mm]});
            skLineSegment(sketch, "E295", {"start": v(-0.84, -9.87) * mm, "end": v(-0.61, -9.92) * mm});
            skLineSegment(sketch, "E296", {"start": v(-0.61, -9.92) * mm, "end": v(-0.28, -9.94) * mm});
            skFitSpline(sketch, "E297", {"points": [v(-0.28, -9.94) * mm, v(-0.1, -9.96) * mm, v(0.1, -9.96) * mm, v(0.17, -9.96) * mm]});
            skFitSpline(sketch, "E298", {"points": [v(0.17, -9.96) * mm, v(0.23, -9.95) * mm, v(0.37, -9.94) * mm, v(0.48, -9.93) * mm]});
            skLineSegment(sketch, "E299", {"start": v(0.48, -9.93) * mm, "end": v(0.48, -9.93) * mm});
            skFitSpline(sketch, "E300", {"points": [v(0.44, -6.24) * mm, v(0.34, -6.22) * mm, v(0.2, -6.16) * mm, v(0.13, -6.13) * mm]});
            skLineSegment(sketch, "E301", {"start": v(0.13, -6.13) * mm, "end": v(0, -6.06) * mm});
            skLineSegment(sketch, "E302", {"start": v(0, -6.06) * mm, "end": v(-0.21, -6.15) * mm});
            skLineSegment(sketch, "E303", {"start": v(-0.21, -6.15) * mm, "end": v(-0.41, -6.24) * mm});
            skLineSegment(sketch, "E304", {"start": v(-0.41, -6.24) * mm, "end": v(-0.66, -6.25) * mm});
            skLineSegment(sketch, "E305", {"start": v(-0.66, -6.25) * mm, "end": v(-0.91, -6.27) * mm});
            skLineSegment(sketch, "E306", {"start": v(-0.91, -6.27) * mm, "end": v(-1.1, -6.2) * mm});
            skLineSegment(sketch, "E307", {"start": v(-1.1, -6.2) * mm, "end": v(-1.29, -6.13) * mm});
            skLineSegment(sketch, "E308", {"start": v(-1.29, -6.13) * mm, "end": v(-1.58, -5.94) * mm});
            skFitSpline(sketch, "E309", {"points": [v(-1.58, -5.94) * mm, v(-1.74, -5.84) * mm, v(-1.92, -5.73) * mm, v(-1.98, -5.7) * mm]});
            skLineSegment(sketch, "E310", {"start": v(-1.98, -5.7) * mm, "end": v(-2.1, -5.65) * mm});
            skLineSegment(sketch, "E311", {"start": v(-2.1, -5.65) * mm, "end": v(-2.1, -5.6) * mm});
            skLineSegment(sketch, "E312", {"start": v(-2.1, -5.6) * mm, "end": v(-2.1, -5.56) * mm});
            skLineSegment(sketch, "E313", {"start": v(-2.1, -5.56) * mm, "end": v(-2.06, -5.56) * mm});
            skFitSpline(sketch, "E314", {"points": [v(-2.06, -5.56) * mm, v(-2.05, -5.56) * mm, v(-1.9, -5.65) * mm, v(-1.74, -5.75) * mm]});
            skFitSpline(sketch, "E315", {"points": [v(-1.74, -5.75) * mm, v(-1.58, -5.85) * mm, v(-1.33, -5.99) * mm, v(-1.2, -6.05) * mm]});
            skLineSegment(sketch, "E316", {"start": v(-1.2, -6.05) * mm, "end": v(-0.95, -6.17) * mm});
            skLineSegment(sketch, "E317", {"start": v(-0.95, -6.17) * mm, "end": v(-0.73, -6.18) * mm});
            skLineSegment(sketch, "E318", {"start": v(-0.73, -6.18) * mm, "end": v(-0.51, -6.18) * mm});
            skLineSegment(sketch, "E319", {"start": v(-0.51, -6.18) * mm, "end": v(-0.34, -6.11) * mm});
            skLineSegment(sketch, "E320", {"start": v(-0.34, -6.11) * mm, "end": v(-0.16, -6.05) * mm});
            skLineSegment(sketch, "E321", {"start": v(-0.16, -6.05) * mm, "end": v(-0.1, -5.98) * mm});
            skLineSegment(sketch, "E322", {"start": v(-0.1, -5.98) * mm, "end": v(-0.05, -5.92) * mm});
            skLineSegment(sketch, "E323", {"start": v(-0.05, -5.92) * mm, "end": v(-0.04, -5.03) * mm});
            skLineSegment(sketch, "E324", {"start": v(-0.04, -5.03) * mm, "end": v(-0.03, -4.14) * mm});
            skLineSegment(sketch, "E325", {"start": v(-0.03, -4.14) * mm, "end": v(-0.6, -3.47) * mm});
            skFitSpline(sketch, "E326", {"points": [v(-0.6, -3.47) * mm, v(-0.9, -3.1) * mm, v(-1.17, -2.79) * mm, v(-1.18, -2.76) * mm]});
            skLineSegment(sketch, "E327", {"start": v(-1.18, -2.76) * mm, "end": v(-1.2, -2.72) * mm});
            skLineSegment(sketch, "E328", {"start": v(-1.2, -2.72) * mm, "end": v(-1, -2.54) * mm});
            skLineSegment(sketch, "E329", {"start": v(-1, -2.54) * mm, "end": v(-0.78, -2.37) * mm});
            skLineSegment(sketch, "E330", {"start": v(-0.78, -2.37) * mm, "end": v(-0.63, -2.3) * mm});
            skFitSpline(sketch, "E331", {"points": [v(-0.63, -2.3) * mm, v(-0.55, -2.25) * mm, v(-0.4, -2.2) * mm, v(-0.3, -2.16) * mm]});
            skLineSegment(sketch, "E332", {"start": v(-0.3, -2.16) * mm, "end": v(-0.12, -2.11) * mm});
            skLineSegment(sketch, "E333", {"start": v(-0.12, -2.11) * mm, "end": v(0.04, -2.11) * mm});
            skLineSegment(sketch, "E334", {"start": v(0.04, -2.11) * mm, "end": v(0.2, -2.11) * mm});
            skLineSegment(sketch, "E335", {"start": v(0.2, -2.11) * mm, "end": v(0.26, -2.14) * mm});
            skFitSpline(sketch, "E336", {"points": [v(0.26, -2.14) * mm, v(0.3, -2.16) * mm, v(0.43, -2.22) * mm, v(0.57, -2.29) * mm]});
            skLineSegment(sketch, "E337", {"start": v(0.57, -2.29) * mm, "end": v(0.82, -2.4) * mm});
            skLineSegment(sketch, "E338", {"start": v(0.82, -2.4) * mm, "end": v(1.01, -2.58) * mm});
            skLineSegment(sketch, "E339", {"start": v(1.01, -2.58) * mm, "end": v(1.2, -2.76) * mm});
            skLineSegment(sketch, "E340", {"start": v(1.2, -2.76) * mm, "end": v(0.64, -3.45) * mm});
            skLineSegment(sketch, "E341", {"start": v(0.64, -3.45) * mm, "end": v(0.07, -4.14) * mm});
            skLineSegment(sketch, "E342", {"start": v(0.07, -4.14) * mm, "end": v(0.07, -5) * mm});
            skLineSegment(sketch, "E343", {"start": v(0.07, -5) * mm, "end": v(0.07, -5.88) * mm});
            skLineSegment(sketch, "E344", {"start": v(0.07, -5.88) * mm, "end": v(0.09, -5.95) * mm});
            skLineSegment(sketch, "E345", {"start": v(0.09, -5.95) * mm, "end": v(0.1, -6.02) * mm});
            skLineSegment(sketch, "E346", {"start": v(0.1, -6.02) * mm, "end": v(0.28, -6.1) * mm});
            skLineSegment(sketch, "E347", {"start": v(0.28, -6.1) * mm, "end": v(0.45, -6.17) * mm});
            skLineSegment(sketch, "E348", {"start": v(0.45, -6.17) * mm, "end": v(0.64, -6.19) * mm});
            skLineSegment(sketch, "E349", {"start": v(0.64, -6.19) * mm, "end": v(0.83, -6.2) * mm});
            skLineSegment(sketch, "E350", {"start": v(0.83, -6.2) * mm, "end": v(1, -6.15) * mm});
            skLineSegment(sketch, "E351", {"start": v(1, -6.15) * mm, "end": v(1.18, -6.09) * mm});
            skLineSegment(sketch, "E352", {"start": v(1.18, -6.09) * mm, "end": v(1.58, -5.84) * mm});
            skLineSegment(sketch, "E353", {"start": v(1.58, -5.84) * mm, "end": v(1.98, -5.6) * mm});
            skLineSegment(sketch, "E354", {"start": v(1.98, -5.6) * mm, "end": v(2.04, -5.6) * mm});
            skLineSegment(sketch, "E355", {"start": v(2.04, -5.6) * mm, "end": v(2.1, -5.6) * mm});
            skLineSegment(sketch, "E356", {"start": v(2.1, -5.6) * mm, "end": v(2.1, -5.63) * mm});
            skFitSpline(sketch, "E357", {"points": [v(2.1, -5.63) * mm, v(2.1, -5.65) * mm, v(2.08, -5.66) * mm, v(2.07, -5.66) * mm]});
            skFitSpline(sketch, "E358", {"points": [v(2.07, -5.66) * mm, v(2.05, -5.66) * mm, v(1.87, -5.77) * mm, v(1.67, -5.9) * mm]});
            skLineSegment(sketch, "E359", {"start": v(1.67, -5.9) * mm, "end": v(1.3, -6.13) * mm});
            skLineSegment(sketch, "E360", {"start": v(1.3, -6.13) * mm, "end": v(1.13, -6.2) * mm});
            skLineSegment(sketch, "E361", {"start": v(1.13, -6.2) * mm, "end": v(0.96, -6.26) * mm});
            skLineSegment(sketch, "E362", {"start": v(0.96, -6.26) * mm, "end": v(0.79, -6.28) * mm});
            skLineSegment(sketch, "E363", {"start": v(0.79, -6.28) * mm, "end": v(0.62, -6.3) * mm});
            skLineSegment(sketch, "E364", {"start": v(0.62, -6.3) * mm, "end": v(0.44, -6.24) * mm});
            skFitSpline(sketch, "E365", {"points": [v(0.55, -3.42) * mm, v(0.82, -3.09) * mm, v(1.05, -2.8) * mm, v(1.05, -2.78) * mm]});
            skLineSegment(sketch, "E366", {"start": v(1.05, -2.78) * mm, "end": v(1.07, -2.75) * mm});
            skLineSegment(sketch, "E367", {"start": v(1.07, -2.75) * mm, "end": v(0.9, -2.6) * mm});
            skLineSegment(sketch, "E368", {"start": v(0.9, -2.6) * mm, "end": v(0.74, -2.46) * mm});
            skLineSegment(sketch, "E369", {"start": v(0.74, -2.46) * mm, "end": v(0.55, -2.37) * mm});
            skLineSegment(sketch, "E370", {"start": v(0.55, -2.37) * mm, "end": v(0.37, -2.27) * mm});
            skLineSegment(sketch, "E371", {"start": v(0.37, -2.27) * mm, "end": v(0.18, -2.24) * mm});
            skLineSegment(sketch, "E372", {"start": v(0.18, -2.24) * mm, "end": v(0, -2.2) * mm});
            skLineSegment(sketch, "E373", {"start": v(0, -2.2) * mm, "end": v(-0.2, -2.24) * mm});
            skLineSegment(sketch, "E374", {"start": v(-0.2, -2.24) * mm, "end": v(-0.4, -2.27) * mm});
            skLineSegment(sketch, "E375", {"start": v(-0.4, -2.27) * mm, "end": v(-0.59, -2.38) * mm});
            skLineSegment(sketch, "E376", {"start": v(-0.59, -2.38) * mm, "end": v(-0.78, -2.48) * mm});
            skLineSegment(sketch, "E377", {"start": v(-0.78, -2.48) * mm, "end": v(-0.94, -2.62) * mm});
            skLineSegment(sketch, "E378", {"start": v(-0.94, -2.62) * mm, "end": v(-1.1, -2.76) * mm});
            skLineSegment(sketch, "E379", {"start": v(-1.1, -2.76) * mm, "end": v(-0.54, -3.4) * mm});
            skFitSpline(sketch, "E380", {"points": [v(-0.54, -3.4) * mm, v(-0.24, -3.75) * mm, v(0.02, -4.04) * mm, v(0.03, -4.03) * mm]});
            skFitSpline(sketch, "E381", {"points": [v(0.03, -4.03) * mm, v(0.04, -4.03) * mm, v(0.27, -3.76) * mm, v(0.55, -3.42) * mm]});
            skLineSegment(sketch, "E382", {"start": v(-3.64, -4.9) * mm, "end": v(-3.66, -4.86) * mm});
            skLineSegment(sketch, "E383", {"start": v(-3.66, -4.86) * mm, "end": v(-3.58, -4.8) * mm});
            skFitSpline(sketch, "E384", {"points": [v(-3.58, -4.8) * mm, v(-3.45, -4.7) * mm, v(-3.05, -4.51) * mm, v(-2.77, -4.43) * mm]});
            skFitSpline(sketch, "E385", {"points": [v(-2.77, -4.43) * mm, v(-2.54, -4.35) * mm, v(-1.96, -4.24) * mm, v(-1.84, -4.24) * mm]});
            skLineSegment(sketch, "E386", {"start": v(-1.84, -4.24) * mm, "end": v(-1.8, -4.24) * mm});
            skLineSegment(sketch, "E387", {"start": v(-1.8, -4.24) * mm, "end": v(-1.8, -4.28) * mm});
            skLineSegment(sketch, "E388", {"start": v(-1.8, -4.28) * mm, "end": v(-1.8, -4.32) * mm});
            skLineSegment(sketch, "E389", {"start": v(-1.8, -4.32) * mm, "end": v(-2.08, -4.36) * mm});
            skLineSegment(sketch, "E390", {"start": v(-2.08, -4.36) * mm, "end": v(-2.37, -4.4) * mm});
            skLineSegment(sketch, "E391", {"start": v(-2.37, -4.4) * mm, "end": v(-2.67, -4.49) * mm});
            skLineSegment(sketch, "E392", {"start": v(-2.67, -4.49) * mm, "end": v(-2.97, -4.57) * mm});
            skLineSegment(sketch, "E393", {"start": v(-2.97, -4.57) * mm, "end": v(-3.24, -4.7) * mm});
            skFitSpline(sketch, "E394", {"points": [v(-3.24, -4.7) * mm, v(-3.38, -4.78) * mm, v(-3.53, -4.86) * mm, v(-3.56, -4.89) * mm]});
            skLineSegment(sketch, "E395", {"start": v(-3.56, -4.89) * mm, "end": v(-3.61, -4.94) * mm});
            skLineSegment(sketch, "E396", {"start": v(-3.61, -4.94) * mm, "end": v(-3.64, -4.9) * mm});
            skLineSegment(sketch, "E397", {"start": v(3.36, -4.78) * mm, "end": v(3.12, -4.64) * mm});
            skLineSegment(sketch, "E398", {"start": v(3.12, -4.64) * mm, "end": v(2.81, -4.54) * mm});
            skLineSegment(sketch, "E399", {"start": v(2.81, -4.54) * mm, "end": v(2.5, -4.44) * mm});
            skLineSegment(sketch, "E400", {"start": v(2.5, -4.44) * mm, "end": v(2.15, -4.38) * mm});
            skLineSegment(sketch, "E401", {"start": v(2.15, -4.38) * mm, "end": v(1.8, -4.32) * mm});
            skLineSegment(sketch, "E402", {"start": v(1.8, -4.32) * mm, "end": v(1.8, -4.28) * mm});
            skLineSegment(sketch, "E403", {"start": v(1.8, -4.28) * mm, "end": v(1.8, -4.23) * mm});
            skLineSegment(sketch, "E404", {"start": v(1.8, -4.23) * mm, "end": v(1.9, -4.25) * mm});
            skFitSpline(sketch, "E405", {"points": [v(1.9, -4.25) * mm, v(1.96, -4.26) * mm, v(2.14, -4.3) * mm, v(2.3, -4.32) * mm]});
            skLineSegment(sketch, "E406", {"start": v(2.3, -4.32) * mm, "end": v(2.6, -4.37) * mm});
            skLineSegment(sketch, "E407", {"start": v(2.6, -4.37) * mm, "end": v(2.88, -4.47) * mm});
            skLineSegment(sketch, "E408", {"start": v(2.88, -4.47) * mm, "end": v(3.17, -4.57) * mm});
            skLineSegment(sketch, "E409", {"start": v(3.17, -4.57) * mm, "end": v(3.41, -4.7) * mm});
            skFitSpline(sketch, "E410", {"points": [v(3.41, -4.7) * mm, v(3.64, -4.84) * mm, v(3.69, -4.88) * mm, v(3.63, -4.9) * mm]});
            skLineSegment(sketch, "E411", {"start": v(3.63, -4.9) * mm, "end": v(3.6, -4.92) * mm});
            skLineSegment(sketch, "E412", {"start": v(3.6, -4.92) * mm, "end": v(3.36, -4.78) * mm});
            skLineSegment(sketch, "E413", {"start": v(-4.77, -4.43) * mm, "end": v(-4.8, -4.39) * mm});
            skLineSegment(sketch, "E414", {"start": v(-4.8, -4.39) * mm, "end": v(-4.66, -4.28) * mm});
            skLineSegment(sketch, "E415", {"start": v(-4.66, -4.28) * mm, "end": v(-4.53, -4.17) * mm});
            skLineSegment(sketch, "E416", {"start": v(-4.53, -4.17) * mm, "end": v(-4.27, -4.04) * mm});
            skLineSegment(sketch, "E417", {"start": v(-4.27, -4.04) * mm, "end": v(-4, -3.9) * mm});
            skLineSegment(sketch, "E418", {"start": v(-4, -3.9) * mm, "end": v(-3.7, -3.82) * mm});
            skFitSpline(sketch, "E419", {"points": [v(-3.7, -3.82) * mm, v(-3.39, -3.73) * mm, v(-2.68, -3.6) * mm, v(-2.33, -3.55) * mm]});
            skLineSegment(sketch, "E420", {"start": v(-2.33, -3.55) * mm, "end": v(-2.12, -3.53) * mm});
            skLineSegment(sketch, "E421", {"start": v(-2.12, -3.53) * mm, "end": v(-2.12, -3.57) * mm});
            skFitSpline(sketch, "E422", {"points": [v(-2.12, -3.57) * mm, v(-2.12, -3.59) * mm, v(-2.13, -3.6) * mm, v(-2.13, -3.6) * mm]});
            skFitSpline(sketch, "E423", {"points": [v(-2.13, -3.6) * mm, v(-2.14, -3.6) * mm, v(-2.4, -3.65) * mm, v(-2.72, -3.7) * mm]});
            skLineSegment(sketch, "E424", {"start": v(-2.72, -3.7) * mm, "end": v(-3.3, -3.8) * mm});
            skLineSegment(sketch, "E425", {"start": v(-3.3, -3.8) * mm, "end": v(-3.62, -3.89) * mm});
            skLineSegment(sketch, "E426", {"start": v(-3.62, -3.89) * mm, "end": v(-3.93, -3.97) * mm});
            skLineSegment(sketch, "E427", {"start": v(-3.93, -3.97) * mm, "end": v(-4.2, -4.1) * mm});
            skLineSegment(sketch, "E428", {"start": v(-4.2, -4.1) * mm, "end": v(-4.46, -4.23) * mm});
            skLineSegment(sketch, "E429", {"start": v(-4.46, -4.23) * mm, "end": v(-4.6, -4.35) * mm});
            skLineSegment(sketch, "E430", {"start": v(-4.6, -4.35) * mm, "end": v(-4.74, -4.47) * mm});
            skLineSegment(sketch, "E431", {"start": v(-4.74, -4.47) * mm, "end": v(-4.77, -4.43) * mm});
            skFitSpline(sketch, "E432", {"points": [v(4.68, -4.42) * mm, v(4.66, -4.4) * mm, v(4.56, -4.32) * mm, v(4.47, -4.25) * mm]});
            skLineSegment(sketch, "E433", {"start": v(4.47, -4.25) * mm, "end": v(4.29, -4.14) * mm});
            skLineSegment(sketch, "E434", {"start": v(4.29, -4.14) * mm, "end": v(4.05, -4.04) * mm});
            skFitSpline(sketch, "E435", {"points": [v(4.05, -4.04) * mm, v(3.72, -3.9) * mm, v(3.34, -3.82) * mm, v(2.7, -3.7) * mm]});
            skLineSegment(sketch, "E436", {"start": v(2.7, -3.7) * mm, "end": v(2.15, -3.61) * mm});
            skLineSegment(sketch, "E437", {"start": v(2.15, -3.61) * mm, "end": v(2.13, -3.58) * mm});
            skLineSegment(sketch, "E438", {"start": v(2.13, -3.58) * mm, "end": v(2.12, -3.54) * mm});
            skLineSegment(sketch, "E439", {"start": v(2.12, -3.54) * mm, "end": v(2.17, -3.54) * mm});
            skFitSpline(sketch, "E440", {"points": [v(2.17, -3.54) * mm, v(2.2, -3.54) * mm, v(2.48, -3.58) * mm, v(2.8, -3.64) * mm]});
            skLineSegment(sketch, "E441", {"start": v(2.8, -3.64) * mm, "end": v(3.37, -3.73) * mm});
            skLineSegment(sketch, "E442", {"start": v(3.37, -3.73) * mm, "end": v(3.67, -3.82) * mm});
            skLineSegment(sketch, "E443", {"start": v(3.67, -3.82) * mm, "end": v(3.97, -3.9) * mm});
            skLineSegment(sketch, "E444", {"start": v(3.97, -3.9) * mm, "end": v(4.27, -4.05) * mm});
            skLineSegment(sketch, "E445", {"start": v(4.27, -4.05) * mm, "end": v(4.57, -4.2) * mm});
            skLineSegment(sketch, "E446", {"start": v(4.57, -4.2) * mm, "end": v(4.68, -4.3) * mm});
            skLineSegment(sketch, "E447", {"start": v(4.68, -4.3) * mm, "end": v(4.8, -4.4) * mm});
            skLineSegment(sketch, "E448", {"start": v(4.8, -4.4) * mm, "end": v(4.76, -4.43) * mm});
            skLineSegment(sketch, "E449", {"start": v(4.76, -4.43) * mm, "end": v(4.73, -4.47) * mm});
            skLineSegment(sketch, "E450", {"start": v(4.73, -4.47) * mm, "end": v(4.68, -4.42) * mm});
            skLineSegment(sketch, "E451", {"start": v(-6.15, -3.83) * mm, "end": v(-6.17, -3.78) * mm});
            skLineSegment(sketch, "E452", {"start": v(-6.17, -3.78) * mm, "end": v(-6.11, -3.73) * mm});
            skFitSpline(sketch, "E453", {"points": [v(-6.11, -3.73) * mm, v(-6.03, -3.65) * mm, v(-5.93, -3.6) * mm, v(-5.53, -3.47) * mm]});
            skFitSpline(sketch, "E454", {"points": [v(-5.53, -3.47) * mm, v(-5.04, -3.3) * mm, v(-4.23, -3.06) * mm, v(-3.72, -2.96) * mm]});
            skLineSegment(sketch, "E455", {"start": v(-3.72, -2.96) * mm, "end": v(-3.3, -2.87) * mm});
            skLineSegment(sketch, "E456", {"start": v(-3.3, -2.87) * mm, "end": v(-2.96, -2.85) * mm});
            skLineSegment(sketch, "E457", {"start": v(-2.96, -2.85) * mm, "end": v(-2.62, -2.83) * mm});
            skLineSegment(sketch, "E458", {"start": v(-2.62, -2.83) * mm, "end": v(-2.64, -2.88) * mm});
            skLineSegment(sketch, "E459", {"start": v(-2.64, -2.88) * mm, "end": v(-2.66, -2.92) * mm});
            skLineSegment(sketch, "E460", {"start": v(-2.66, -2.92) * mm, "end": v(-2.9, -2.93) * mm});
            skFitSpline(sketch, "E461", {"points": [v(-2.9, -2.93) * mm, v(-3.03, -2.94) * mm, v(-3.27, -2.96) * mm, v(-3.43, -3) * mm]});
            skFitSpline(sketch, "E462", {"points": [v(-3.43, -3) * mm, v(-4.13, -3.1) * mm, v(-5.55, -3.52) * mm, v(-5.94, -3.72) * mm]});
            skLineSegment(sketch, "E463", {"start": v(-5.94, -3.72) * mm, "end": v(-6.1, -3.8) * mm});
            skLineSegment(sketch, "E464", {"start": v(-6.1, -3.8) * mm, "end": v(-6.12, -3.84) * mm});
            skLineSegment(sketch, "E465", {"start": v(-6.12, -3.84) * mm, "end": v(-6.13, -3.88) * mm});
            skLineSegment(sketch, "E466", {"start": v(-6.13, -3.88) * mm, "end": v(-6.15, -3.83) * mm});
            skLineSegment(sketch, "E467", {"start": v(6.11, -3.84) * mm, "end": v(6.11, -3.81) * mm});
            skLineSegment(sketch, "E468", {"start": v(6.11, -3.81) * mm, "end": v(5.88, -3.7) * mm});
            skFitSpline(sketch, "E469", {"points": [v(5.88, -3.7) * mm, v(5.43, -3.5) * mm, v(4.49, -3.21) * mm, v(3.72, -3.05) * mm]});
            skLineSegment(sketch, "E470", {"start": v(3.72, -3.05) * mm, "end": v(3.3, -2.97) * mm});
            skLineSegment(sketch, "E471", {"start": v(3.3, -2.97) * mm, "end": v(2.98, -2.95) * mm});
            skLineSegment(sketch, "E472", {"start": v(2.98, -2.95) * mm, "end": v(2.65, -2.92) * mm});
            skLineSegment(sketch, "E473", {"start": v(2.65, -2.92) * mm, "end": v(2.63, -2.88) * mm});
            skLineSegment(sketch, "E474", {"start": v(2.63, -2.88) * mm, "end": v(2.62, -2.84) * mm});
            skLineSegment(sketch, "E475", {"start": v(2.62, -2.84) * mm, "end": v(2.82, -2.84) * mm});
            skLineSegment(sketch, "E476", {"start": v(2.82, -2.84) * mm, "end": v(3.02, -2.84) * mm});
            skLineSegment(sketch, "E477", {"start": v(3.02, -2.84) * mm, "end": v(3.4, -2.9) * mm});
            skFitSpline(sketch, "E478", {"points": [v(3.4, -2.9) * mm, v(4.18, -3.04) * mm, v(5.38, -3.38) * mm, v(5.9, -3.62) * mm]});
            skLineSegment(sketch, "E479", {"start": v(5.9, -3.62) * mm, "end": v(6.14, -3.73) * mm});
            skLineSegment(sketch, "E480", {"start": v(6.14, -3.73) * mm, "end": v(6.14, -3.8) * mm});
            skFitSpline(sketch, "E481", {"points": [v(6.14, -3.8) * mm, v(6.14, -3.84) * mm, v(6.14, -3.87) * mm, v(6.13, -3.87) * mm]});
            skFitSpline(sketch, "E482", {"points": [v(6.13, -3.87) * mm, v(6.12, -3.87) * mm, v(6.11, -3.86) * mm, v(6.11, -3.84) * mm]});
            skLineSegment(sketch, "E483", {"start": v(-4.38, -1.37) * mm, "end": v(-4.38, -1.37) * mm});
            skFitSpline(sketch, "E484", {"points": [v(-3.58, -1.3) * mm, v(-2.74, -1.22) * mm, v(-2.27, -1.13) * mm, v(-1.67, -0.96) * mm]});
            skLineSegment(sketch, "E485", {"start": v(-1.67, -0.96) * mm, "end": v(-1.59, -0.94) * mm});
            skLineSegment(sketch, "E486", {"start": v(-1.59, -0.94) * mm, "end": v(-1.6, -0.9) * mm});
            skFitSpline(sketch, "E487", {"points": [v(-1.6, -0.9) * mm, v(-1.61, -0.88) * mm, v(-1.92, -0.4) * mm, v(-2.3, 0.17) * mm]});
            skLineSegment(sketch, "E488", {"start": v(-2.3, 0.17) * mm, "end": v(-2.98, 1.2) * mm});
            skLineSegment(sketch, "E489", {"start": v(-2.98, 1.2) * mm, "end": v(-3.2, 1.29) * mm});
            skLineSegment(sketch, "E490", {"start": v(-3.2, 1.29) * mm, "end": v(-3.41, 1.37) * mm});
            skLineSegment(sketch, "E491", {"start": v(-3.41, 1.37) * mm, "end": v(-3.63, 1.4) * mm});
            skLineSegment(sketch, "E492", {"start": v(-3.63, 1.4) * mm, "end": v(-3.85, 1.44) * mm});
            skLineSegment(sketch, "E493", {"start": v(-3.85, 1.44) * mm, "end": v(-4.08, 1.4) * mm});
            skLineSegment(sketch, "E494", {"start": v(-4.08, 1.4) * mm, "end": v(-4.32, 1.38) * mm});
            skLineSegment(sketch, "E495", {"start": v(-4.32, 1.38) * mm, "end": v(-4.58, 1.3) * mm});
            skLineSegment(sketch, "E496", {"start": v(-4.58, 1.3) * mm, "end": v(-4.83, 1.2) * mm});
            skLineSegment(sketch, "E497", {"start": v(-4.83, 1.2) * mm, "end": v(-5.15, 1.04) * mm});
            skFitSpline(sketch, "E498", {"points": [v(-5.15, 1.04) * mm, v(-5.54, 0.84) * mm, v(-6.34, 0.34) * mm, v(-6.34, 0.3) * mm]});
            skFitSpline(sketch, "E499", {"points": [v(-6.34, 0.3) * mm, v(-6.34, 0.25) * mm, v(-6.02, -0.14) * mm, v(-5.76, -0.4) * mm]});
            skLineSegment(sketch, "E500", {"start": v(-5.76, -0.4) * mm, "end": v(-5.49, -0.67) * mm});
            skLineSegment(sketch, "E501", {"start": v(-5.49, -0.67) * mm, "end": v(-5.23, -0.84) * mm});
            skFitSpline(sketch, "E502", {"points": [v(-5.23, -0.84) * mm, v(-4.88, -1.08) * mm, v(-4.32, -1.34) * mm, v(-4.15, -1.34) * mm]});
            skFitSpline(sketch, "E503", {"points": [v(-4.15, -1.34) * mm, v(-4.12, -1.35) * mm, v(-3.86, -1.32) * mm, v(-3.58, -1.3) * mm]});
            skFitSpline(sketch, "E504", {"points": [v(-4.28, -0.93) * mm, v(-4.35, -0.9) * mm, v(-4.48, -0.85) * mm, v(-4.57, -0.8) * mm]});
            skLineSegment(sketch, "E505", {"start": v(-4.57, -0.8) * mm, "end": v(-4.74, -0.72) * mm});
            skLineSegment(sketch, "E506", {"start": v(-4.74, -0.72) * mm, "end": v(-4.87, -0.57) * mm});
            skLineSegment(sketch, "E507", {"start": v(-4.87, -0.57) * mm, "end": v(-5, -0.41) * mm});
            skLineSegment(sketch, "E508", {"start": v(-5, -0.41) * mm, "end": v(-5.05, -0.25) * mm});
            skLineSegment(sketch, "E509", {"start": v(-5.05, -0.25) * mm, "end": v(-5.09, -0.08) * mm});
            skLineSegment(sketch, "E510", {"start": v(-5.09, -0.08) * mm, "end": v(-5.07, 0.11) * mm});
            skLineSegment(sketch, "E511", {"start": v(-5.07, 0.11) * mm, "end": v(-5.05, 0.3) * mm});
            skLineSegment(sketch, "E512", {"start": v(-5.05, 0.3) * mm, "end": v(-4.98, 0.44) * mm});
            skLineSegment(sketch, "E513", {"start": v(-4.98, 0.44) * mm, "end": v(-4.9, 0.59) * mm});
            skLineSegment(sketch, "E514", {"start": v(-4.9, 0.59) * mm, "end": v(-4.76, 0.73) * mm});
            skLineSegment(sketch, "E515", {"start": v(-4.76, 0.73) * mm, "end": v(-4.62, 0.87) * mm});
            skLineSegment(sketch, "E516", {"start": v(-4.62, 0.87) * mm, "end": v(-4.43, 0.93) * mm});
            skLineSegment(sketch, "E517", {"start": v(-4.43, 0.93) * mm, "end": v(-4.23, 0.99) * mm});
            skLineSegment(sketch, "E518", {"start": v(-4.23, 0.99) * mm, "end": v(-3.92, 0.99) * mm});
            skLineSegment(sketch, "E519", {"start": v(-3.92, 0.99) * mm, "end": v(-3.6, 1) * mm});
            skLineSegment(sketch, "E520", {"start": v(-3.6, 1) * mm, "end": v(-3.44, 0.91) * mm});
            skLineSegment(sketch, "E521", {"start": v(-3.44, 0.91) * mm, "end": v(-3.29, 0.84) * mm});
            skLineSegment(sketch, "E522", {"start": v(-3.29, 0.84) * mm, "end": v(-3.2, 0.73) * mm});
            skFitSpline(sketch, "E523", {"points": [v(-3.2, 0.73) * mm, v(-3.15, 0.68) * mm, v(-3.08, 0.57) * mm, v(-3.05, 0.49) * mm]});
            skLineSegment(sketch, "E524", {"start": v(-3.05, 0.49) * mm, "end": v(-3, 0.35) * mm});
            skLineSegment(sketch, "E525", {"start": v(-3, 0.35) * mm, "end": v(-2.95, 0.1) * mm});
            skLineSegment(sketch, "E526", {"start": v(-2.95, 0.1) * mm, "end": v(-2.91, -0.17) * mm});
            skLineSegment(sketch, "E527", {"start": v(-2.91, -0.17) * mm, "end": v(-3.02, -0.4) * mm});
            skFitSpline(sketch, "E528", {"points": [v(-3.02, -0.4) * mm, v(-3.08, -0.52) * mm, v(-3.16, -0.66) * mm, v(-3.21, -0.72) * mm]});
            skLineSegment(sketch, "E529", {"start": v(-3.21, -0.72) * mm, "end": v(-3.3, -0.82) * mm});
            skLineSegment(sketch, "E530", {"start": v(-3.3, -0.82) * mm, "end": v(-3.47, -0.9) * mm});
            skLineSegment(sketch, "E531", {"start": v(-3.47, -0.9) * mm, "end": v(-3.63, -0.98) * mm});
            skLineSegment(sketch, "E532", {"start": v(-3.63, -0.98) * mm, "end": v(-3.9, -0.98) * mm});
            skLineSegment(sketch, "E533", {"start": v(-3.9, -0.98) * mm, "end": v(-4.17, -0.98) * mm});
            skLineSegment(sketch, "E534", {"start": v(-4.17, -0.98) * mm, "end": v(-4.28, -0.93) * mm});
            skLineSegment(sketch, "E535", {"start": v(-4.28, -0.93) * mm, "end": v(-4.28, -0.93) * mm});
            skLineSegment(sketch, "E536", {"start": v(-3.66, -0.88) * mm, "end": v(-3.5, -0.84) * mm});
            skLineSegment(sketch, "E537", {"start": v(-3.5, -0.84) * mm, "end": v(-3.36, -0.73) * mm});
            skLineSegment(sketch, "E538", {"start": v(-3.36, -0.73) * mm, "end": v(-3.22, -0.61) * mm});
            skLineSegment(sketch, "E539", {"start": v(-3.22, -0.61) * mm, "end": v(-3.12, -0.4) * mm});
            skLineSegment(sketch, "E540", {"start": v(-3.12, -0.4) * mm, "end": v(-3.01, -0.17) * mm});
            skLineSegment(sketch, "E541", {"start": v(-3.01, -0.17) * mm, "end": v(-3.03, 0.03) * mm});
            skLineSegment(sketch, "E542", {"start": v(-3.03, 0.03) * mm, "end": v(-3.05, 0.23) * mm});
            skLineSegment(sketch, "E543", {"start": v(-3.05, 0.23) * mm, "end": v(-3.1, 0.4) * mm});
            skLineSegment(sketch, "E544", {"start": v(-3.1, 0.4) * mm, "end": v(-3.16, 0.56) * mm});
            skLineSegment(sketch, "E545", {"start": v(-3.16, 0.56) * mm, "end": v(-3.3, 0.7) * mm});
            skLineSegment(sketch, "E546", {"start": v(-3.3, 0.7) * mm, "end": v(-3.44, 0.83) * mm});
            skLineSegment(sketch, "E547", {"start": v(-3.44, 0.83) * mm, "end": v(-3.6, 0.88) * mm});
            skLineSegment(sketch, "E548", {"start": v(-3.6, 0.88) * mm, "end": v(-3.75, 0.92) * mm});
            skLineSegment(sketch, "E549", {"start": v(-3.75, 0.92) * mm, "end": v(-4.05, 0.9) * mm});
            skLineSegment(sketch, "E550", {"start": v(-4.05, 0.9) * mm, "end": v(-4.35, 0.88) * mm});
            skLineSegment(sketch, "E551", {"start": v(-4.35, 0.88) * mm, "end": v(-4.5, 0.81) * mm});
            skLineSegment(sketch, "E552", {"start": v(-4.5, 0.81) * mm, "end": v(-4.64, 0.74) * mm});
            skLineSegment(sketch, "E553", {"start": v(-4.64, 0.74) * mm, "end": v(-4.75, 0.63) * mm});
            skFitSpline(sketch, "E554", {"points": [v(-4.75, 0.63) * mm, v(-4.8, 0.56) * mm, v(-4.88, 0.45) * mm, v(-4.92, 0.37) * mm]});
            skLineSegment(sketch, "E555", {"start": v(-4.92, 0.37) * mm, "end": v(-4.99, 0.24) * mm});
            skLineSegment(sketch, "E556", {"start": v(-4.99, 0.24) * mm, "end": v(-4.97, -0.03) * mm});
            skLineSegment(sketch, "E557", {"start": v(-4.97, -0.03) * mm, "end": v(-4.96, -0.3) * mm});
            skLineSegment(sketch, "E558", {"start": v(-4.96, -0.3) * mm, "end": v(-4.87, -0.44) * mm});
            skLineSegment(sketch, "E559", {"start": v(-4.87, -0.44) * mm, "end": v(-4.78, -0.58) * mm});
            skLineSegment(sketch, "E560", {"start": v(-4.78, -0.58) * mm, "end": v(-4.63, -0.67) * mm});
            skFitSpline(sketch, "E561", {"points": [v(-4.63, -0.67) * mm, v(-4.54, -0.72) * mm, v(-4.4, -0.8) * mm, v(-4.29, -0.84) * mm]});
            skLineSegment(sketch, "E562", {"start": v(-4.29, -0.84) * mm, "end": v(-4.1, -0.91) * mm});
            skLineSegment(sketch, "E563", {"start": v(-4.1, -0.91) * mm, "end": v(-3.96, -0.91) * mm});
            skFitSpline(sketch, "E564", {"points": [v(-3.96, -0.91) * mm, v(-3.88, -0.91) * mm, v(-3.75, -0.9) * mm, v(-3.66, -0.88) * mm]});
            skLineSegment(sketch, "E565", {"start": v(-3.66, -0.88) * mm, "end": v(-3.66, -0.88) * mm});
            skFitSpline(sketch, "E566", {"points": [v(-4.02, -0.57) * mm, v(-4.03, -0.56) * mm, v(-4, -0.3) * mm, v(-3.97, 0.01) * mm]});
            skLineSegment(sketch, "E567", {"start": v(-3.97, 0.01) * mm, "end": v(-3.9, 0.58) * mm});
            skLineSegment(sketch, "E568", {"start": v(-3.9, 0.58) * mm, "end": v(-3.86, 0.58) * mm});
            skFitSpline(sketch, "E569", {"points": [v(-3.86, 0.58) * mm, v(-3.8, 0.58) * mm, v(-3.8, 0.62) * mm, v(-3.88, 0) * mm]});
            skFitSpline(sketch, "E570", {"points": [v(-3.88, 0) * mm, v(-3.92, -0.3) * mm, v(-3.95, -0.54) * mm, v(-3.95, -0.56) * mm]});
            skFitSpline(sketch, "E571", {"points": [v(-3.95, -0.56) * mm, v(-3.95, -0.59) * mm, v(-4, -0.6) * mm, v(-4.02, -0.57) * mm]});
            skFitSpline(sketch, "E572", {"points": [v(3.4, -1.38) * mm, v(2.68, -1.3) * mm, v(2.18, -1.21) * mm, v(1.75, -1.08) * mm]});
            skLineSegment(sketch, "E573", {"start": v(1.75, -1.08) * mm, "end": v(1.43, -0.98) * mm});
            skLineSegment(sketch, "E574", {"start": v(1.43, -0.98) * mm, "end": v(1.99, -0.14) * mm});
            skFitSpline(sketch, "E575", {"points": [v(1.99, -0.14) * mm, v(2.3, 0.32) * mm, v(2.62, 0.82) * mm, v(2.72, 0.96) * mm]});
            skLineSegment(sketch, "E576", {"start": v(2.72, 0.96) * mm, "end": v(2.9, 1.23) * mm});
            skLineSegment(sketch, "E577", {"start": v(2.9, 1.23) * mm, "end": v(3.08, 1.32) * mm});
            skFitSpline(sketch, "E578", {"points": [v(3.08, 1.32) * mm, v(3.19, 1.37) * mm, v(3.37, 1.43) * mm, v(3.49, 1.46) * mm]});
            skLineSegment(sketch, "E579", {"start": v(3.49, 1.46) * mm, "end": v(3.7, 1.52) * mm});
            skLineSegment(sketch, "E580", {"start": v(3.7, 1.52) * mm, "end": v(3.97, 1.5) * mm});
            skLineSegment(sketch, "E581", {"start": v(3.97, 1.5) * mm, "end": v(4.23, 1.48) * mm});
            skLineSegment(sketch, "E582", {"start": v(4.23, 1.48) * mm, "end": v(4.52, 1.4) * mm});
            skLineSegment(sketch, "E583", {"start": v(4.52, 1.4) * mm, "end": v(4.8, 1.3) * mm});
            skLineSegment(sketch, "E584", {"start": v(4.8, 1.3) * mm, "end": v(5.18, 1.1) * mm});
            skLineSegment(sketch, "E585", {"start": v(5.18, 1.1) * mm, "end": v(5.56, 0.91) * mm});
            skLineSegment(sketch, "E586", {"start": v(5.56, 0.91) * mm, "end": v(6.01, 0.63) * mm});
            skFitSpline(sketch, "E587", {"points": [v(6.01, 0.63) * mm, v(6.26, 0.47) * mm, v(6.46, 0.34) * mm, v(6.47, 0.33) * mm]});
            skFitSpline(sketch, "E588", {"points": [v(6.47, 0.33) * mm, v(6.48, 0.32) * mm, v(6.4, 0.2) * mm, v(6.29, 0.06) * mm]});
            skLineSegment(sketch, "E589", {"start": v(6.29, 0.06) * mm, "end": v(6.1, -0.2) * mm});
            skLineSegment(sketch, "E590", {"start": v(6.1, -0.2) * mm, "end": v(5.83, -0.47) * mm});
            skLineSegment(sketch, "E591", {"start": v(5.83, -0.47) * mm, "end": v(5.56, -0.74) * mm});
            skLineSegment(sketch, "E592", {"start": v(5.56, -0.74) * mm, "end": v(5.27, -0.93) * mm});
            skLineSegment(sketch, "E593", {"start": v(5.27, -0.93) * mm, "end": v(5, -1.11) * mm});
            skLineSegment(sketch, "E594", {"start": v(5, -1.11) * mm, "end": v(4.76, -1.22) * mm});
            skFitSpline(sketch, "E595", {"points": [v(4.76, -1.22) * mm, v(4.64, -1.28) * mm, v(4.45, -1.35) * mm, v(4.35, -1.38) * mm]});
            skLineSegment(sketch, "E596", {"start": v(4.35, -1.38) * mm, "end": v(4.17, -1.45) * mm});
            skLineSegment(sketch, "E597", {"start": v(4.17, -1.45) * mm, "end": v(4.09, -1.44) * mm});
            skFitSpline(sketch, "E598", {"points": [v(4.09, -1.44) * mm, v(4.04, -1.44) * mm, v(3.73, -1.41) * mm, v(3.4, -1.38) * mm]});
            skLineSegment(sketch, "E599", {"start": v(4.6, -1.2) * mm, "end": v(4.9, -1.07) * mm});
            skLineSegment(sketch, "E600", {"start": v(4.9, -1.07) * mm, "end": v(5.18, -0.88) * mm});
            skLineSegment(sketch, "E601", {"start": v(5.18, -0.88) * mm, "end": v(5.46, -0.69) * mm});
            skLineSegment(sketch, "E602", {"start": v(5.46, -0.69) * mm, "end": v(5.69, -0.48) * mm});
            skLineSegment(sketch, "E603", {"start": v(5.69, -0.48) * mm, "end": v(5.91, -0.28) * mm});
            skLineSegment(sketch, "E604", {"start": v(5.91, -0.28) * mm, "end": v(6.13, 0) * mm});
            skLineSegment(sketch, "E605", {"start": v(6.13, 0) * mm, "end": v(6.35, 0.28) * mm});
            skLineSegment(sketch, "E606", {"start": v(6.35, 0.28) * mm, "end": v(6.32, 0.32) * mm});
            skFitSpline(sketch, "E607", {"points": [v(6.32, 0.32) * mm, v(6.3, 0.34) * mm, v(6.1, 0.46) * mm, v(5.89, 0.6) * mm]});
            skLineSegment(sketch, "E608", {"start": v(5.89, 0.6) * mm, "end": v(5.5, 0.85) * mm});
            skLineSegment(sketch, "E609", {"start": v(5.5, 0.85) * mm, "end": v(5.06, 1.06) * mm});
            skLineSegment(sketch, "E610", {"start": v(5.06, 1.06) * mm, "end": v(4.63, 1.28) * mm});
            skLineSegment(sketch, "E611", {"start": v(4.63, 1.28) * mm, "end": v(4.37, 1.34) * mm});
            skLineSegment(sketch, "E612", {"start": v(4.37, 1.34) * mm, "end": v(4.1, 1.4) * mm});
            skLineSegment(sketch, "E613", {"start": v(4.1, 1.4) * mm, "end": v(3.86, 1.4) * mm});
            skLineSegment(sketch, "E614", {"start": v(3.86, 1.4) * mm, "end": v(3.6, 1.4) * mm});
            skLineSegment(sketch, "E615", {"start": v(3.6, 1.4) * mm, "end": v(3.47, 1.37) * mm});
            skFitSpline(sketch, "E616", {"points": [v(3.47, 1.37) * mm, v(3.4, 1.35) * mm, v(3.25, 1.3) * mm, v(3.15, 1.25) * mm]});
            skLineSegment(sketch, "E617", {"start": v(3.15, 1.25) * mm, "end": v(2.96, 1.17) * mm});
            skLineSegment(sketch, "E618", {"start": v(2.96, 1.17) * mm, "end": v(2.27, 0.13) * mm});
            skFitSpline(sketch, "E619", {"points": [v(2.27, 0.13) * mm, v(1.9, -0.45) * mm, v(1.6, -0.92) * mm, v(1.6, -0.93) * mm]});
            skFitSpline(sketch, "E620", {"points": [v(1.6, -0.93) * mm, v(1.64, -0.97) * mm, v(2.16, -1.1) * mm, v(2.46, -1.16) * mm]});
            skFitSpline(sketch, "E621", {"points": [v(2.46, -1.16) * mm, v(2.64, -1.2) * mm, v(3.02, -1.25) * mm, v(3.32, -1.28) * mm]});
            skLineSegment(sketch, "E622", {"start": v(3.32, -1.28) * mm, "end": v(3.87, -1.34) * mm});
            skLineSegment(sketch, "E623", {"start": v(3.87, -1.34) * mm, "end": v(4.08, -1.33) * mm});
            skLineSegment(sketch, "E624", {"start": v(4.08, -1.33) * mm, "end": v(4.3, -1.32) * mm});
            skLineSegment(sketch, "E625", {"start": v(4.3, -1.32) * mm, "end": v(4.6, -1.2) * mm});
            skLineSegment(sketch, "E626", {"start": v(4.6, -1.2) * mm, "end": v(4.6, -1.2) * mm});
            skFitSpline(sketch, "E627", {"points": [v(3.7, -1) * mm, v(3.67, -0.98) * mm, v(3.59, -0.96) * mm, v(3.52, -0.94) * mm]});
            skLineSegment(sketch, "E628", {"start": v(3.52, -0.94) * mm, "end": v(3.41, -0.9) * mm});
            skLineSegment(sketch, "E629", {"start": v(3.41, -0.9) * mm, "end": v(3.28, -0.79) * mm});
            skLineSegment(sketch, "E630", {"start": v(3.28, -0.79) * mm, "end": v(3.15, -0.67) * mm});
            skLineSegment(sketch, "E631", {"start": v(3.15, -0.67) * mm, "end": v(3.03, -0.44) * mm});
            skLineSegment(sketch, "E632", {"start": v(3.03, -0.44) * mm, "end": v(2.91, -0.2) * mm});
            skLineSegment(sketch, "E633", {"start": v(2.91, -0.2) * mm, "end": v(2.94, 0) * mm});
            skFitSpline(sketch, "E634", {"points": [v(2.94, 0) * mm, v(2.95, 0.11) * mm, v(2.98, 0.28) * mm, v(3, 0.37) * mm]});
            skLineSegment(sketch, "E635", {"start": v(3, 0.37) * mm, "end": v(3.05, 0.53) * mm});
            skLineSegment(sketch, "E636", {"start": v(3.05, 0.53) * mm, "end": v(3.15, 0.67) * mm});
            skLineSegment(sketch, "E637", {"start": v(3.15, 0.67) * mm, "end": v(3.25, 0.8) * mm});
            skLineSegment(sketch, "E638", {"start": v(3.25, 0.8) * mm, "end": v(3.44, 0.9) * mm});
            skLineSegment(sketch, "E639", {"start": v(3.44, 0.9) * mm, "end": v(3.63, 1) * mm});
            skLineSegment(sketch, "E640", {"start": v(3.63, 1) * mm, "end": v(3.92, 0.99) * mm});
            skLineSegment(sketch, "E641", {"start": v(3.92, 0.99) * mm, "end": v(4.22, 0.98) * mm});
            skLineSegment(sketch, "E642", {"start": v(4.22, 0.98) * mm, "end": v(4.4, 0.93) * mm});
            skLineSegment(sketch, "E643", {"start": v(4.4, 0.93) * mm, "end": v(4.59, 0.87) * mm});
            skLineSegment(sketch, "E644", {"start": v(4.59, 0.87) * mm, "end": v(4.74, 0.74) * mm});
            skLineSegment(sketch, "E645", {"start": v(4.74, 0.74) * mm, "end": v(4.89, 0.6) * mm});
            skLineSegment(sketch, "E646", {"start": v(4.89, 0.6) * mm, "end": v(4.98, 0.45) * mm});
            skLineSegment(sketch, "E647", {"start": v(4.98, 0.45) * mm, "end": v(5.06, 0.3) * mm});
            skLineSegment(sketch, "E648", {"start": v(5.06, 0.3) * mm, "end": v(5.06, 0.01) * mm});
            skLineSegment(sketch, "E649", {"start": v(5.06, 0.01) * mm, "end": v(5.06, -0.27) * mm});
            skLineSegment(sketch, "E650", {"start": v(5.06, -0.27) * mm, "end": v(4.97, -0.44) * mm});
            skLineSegment(sketch, "E651", {"start": v(4.97, -0.44) * mm, "end": v(4.87, -0.61) * mm});
            skLineSegment(sketch, "E652", {"start": v(4.87, -0.61) * mm, "end": v(4.7, -0.73) * mm});
            skLineSegment(sketch, "E653", {"start": v(4.7, -0.73) * mm, "end": v(4.53, -0.85) * mm});
            skLineSegment(sketch, "E654", {"start": v(4.53, -0.85) * mm, "end": v(4.3, -0.93) * mm});
            skLineSegment(sketch, "E655", {"start": v(4.3, -0.93) * mm, "end": v(4.07, -1.01) * mm});
            skLineSegment(sketch, "E656", {"start": v(4.07, -1.01) * mm, "end": v(3.92, -1.01) * mm});
            skFitSpline(sketch, "E657", {"points": [v(3.92, -1.01) * mm, v(3.84, -1) * mm, v(3.74, -1) * mm, v(3.7, -1) * mm]});
            skLineSegment(sketch, "E658", {"start": v(3.7, -1) * mm, "end": v(3.7, -1) * mm});
            skLineSegment(sketch, "E659", {"start": v(4.37, -0.8) * mm, "end": v(4.63, -0.7) * mm});
            skLineSegment(sketch, "E660", {"start": v(4.63, -0.7) * mm, "end": v(4.77, -0.56) * mm});
            skLineSegment(sketch, "E661", {"start": v(4.77, -0.56) * mm, "end": v(4.91, -0.42) * mm});
            skLineSegment(sketch, "E662", {"start": v(4.91, -0.42) * mm, "end": v(4.95, -0.28) * mm});
            skLineSegment(sketch, "E663", {"start": v(4.95, -0.28) * mm, "end": v(4.99, -0.14) * mm});
            skLineSegment(sketch, "E664", {"start": v(4.99, -0.14) * mm, "end": v(4.98, 0.08) * mm});
            skLineSegment(sketch, "E665", {"start": v(4.98, 0.08) * mm, "end": v(4.96, 0.3) * mm});
            skLineSegment(sketch, "E666", {"start": v(4.96, 0.3) * mm, "end": v(4.84, 0.49) * mm});
            skLineSegment(sketch, "E667", {"start": v(4.84, 0.49) * mm, "end": v(4.72, 0.67) * mm});
            skLineSegment(sketch, "E668", {"start": v(4.72, 0.67) * mm, "end": v(4.58, 0.76) * mm});
            skLineSegment(sketch, "E669", {"start": v(4.58, 0.76) * mm, "end": v(4.43, 0.84) * mm});
            skLineSegment(sketch, "E670", {"start": v(4.43, 0.84) * mm, "end": v(4.18, 0.88) * mm});
            skLineSegment(sketch, "E671", {"start": v(4.18, 0.88) * mm, "end": v(3.94, 0.92) * mm});
            skLineSegment(sketch, "E672", {"start": v(3.94, 0.92) * mm, "end": v(3.77, 0.9) * mm});
            skLineSegment(sketch, "E673", {"start": v(3.77, 0.9) * mm, "end": v(3.6, 0.88) * mm});
            skLineSegment(sketch, "E674", {"start": v(3.6, 0.88) * mm, "end": v(3.46, 0.81) * mm});
            skLineSegment(sketch, "E675", {"start": v(3.46, 0.81) * mm, "end": v(3.32, 0.75) * mm});
            skLineSegment(sketch, "E676", {"start": v(3.32, 0.75) * mm, "end": v(3.24, 0.63) * mm});
            skLineSegment(sketch, "E677", {"start": v(3.24, 0.63) * mm, "end": v(3.15, 0.52) * mm});
            skLineSegment(sketch, "E678", {"start": v(3.15, 0.52) * mm, "end": v(3.1, 0.38) * mm});
            skFitSpline(sketch, "E679", {"points": [v(3.1, 0.38) * mm, v(3.08, 0.3) * mm, v(3.04, 0.14) * mm, v(3.03, 0.03) * mm]});
            skLineSegment(sketch, "E680", {"start": v(3.03, 0.03) * mm, "end": v(3, -0.17) * mm});
            skLineSegment(sketch, "E681", {"start": v(3, -0.17) * mm, "end": v(3.13, -0.43) * mm});
            skLineSegment(sketch, "E682", {"start": v(3.13, -0.43) * mm, "end": v(3.26, -0.68) * mm});
            skLineSegment(sketch, "E683", {"start": v(3.26, -0.68) * mm, "end": v(3.36, -0.76) * mm});
            skFitSpline(sketch, "E684", {"points": [v(3.36, -0.76) * mm, v(3.42, -0.8) * mm, v(3.52, -0.85) * mm, v(3.58, -0.87) * mm]});
            skLineSegment(sketch, "E685", {"start": v(3.58, -0.87) * mm, "end": v(3.7, -0.91) * mm});
            skLineSegment(sketch, "E686", {"start": v(3.7, -0.91) * mm, "end": v(3.9, -0.91) * mm});
            skLineSegment(sketch, "E687", {"start": v(3.9, -0.91) * mm, "end": v(4.1, -0.92) * mm});
            skLineSegment(sketch, "E688", {"start": v(4.1, -0.92) * mm, "end": v(4.37, -0.8) * mm});
            skLineSegment(sketch, "E689", {"start": v(4.37, -0.8) * mm, "end": v(4.37, -0.8) * mm});
            skFitSpline(sketch, "E690", {"points": [v(3.94, -0.48) * mm, v(3.9, -0.3) * mm, v(3.82, 0.46) * mm, v(3.82, 0.53) * mm]});
            skLineSegment(sketch, "E691", {"start": v(3.82, 0.53) * mm, "end": v(3.82, 0.58) * mm});
            skLineSegment(sketch, "E692", {"start": v(3.82, 0.58) * mm, "end": v(3.86, 0.57) * mm});
            skLineSegment(sketch, "E693", {"start": v(3.86, 0.57) * mm, "end": v(3.9, 0.56) * mm});
            skLineSegment(sketch, "E694", {"start": v(3.9, 0.56) * mm, "end": v(3.96, 0.1) * mm});
            skFitSpline(sketch, "E695", {"points": [v(3.96, 0.1) * mm, v(3.99, -0.16) * mm, v(4.02, -0.42) * mm, v(4.02, -0.48) * mm]});
            skLineSegment(sketch, "E696", {"start": v(4.02, -0.48) * mm, "end": v(4.02, -0.58) * mm});
            skLineSegment(sketch, "E697", {"start": v(4.02, -0.58) * mm, "end": v(3.99, -0.58) * mm});
            skLineSegment(sketch, "E698", {"start": v(3.99, -0.58) * mm, "end": v(3.95, -0.58) * mm});
            skLineSegment(sketch, "E699", {"start": v(3.95, -0.58) * mm, "end": v(3.94, -0.48) * mm});
            skLineSegment(sketch, "E700", {"start": v(3.94, -0.48) * mm, "end": v(3.94, -0.48) * mm});
            skFitSpline(sketch, "E701", {"points": [v(-7.8, 4.87) * mm, v(-7.86, 4.95) * mm, v(-7.96, 5.1) * mm, v(-8.02, 5.21) * mm]});
            skLineSegment(sketch, "E702", {"start": v(-8.02, 5.21) * mm, "end": v(-8.13, 5.4) * mm});
            skLineSegment(sketch, "E703", {"start": v(-8.13, 5.4) * mm, "end": v(-8.25, 5.76) * mm});
            skLineSegment(sketch, "E704", {"start": v(-8.25, 5.76) * mm, "end": v(-8.36, 6.1) * mm});
            skLineSegment(sketch, "E705", {"start": v(-8.36, 6.1) * mm, "end": v(-8.43, 6.49) * mm});
            skFitSpline(sketch, "E706", {"points": [v(-8.43, 6.49) * mm, v(-8.47, 6.7) * mm, v(-8.52, 7.1) * mm, v(-8.55, 7.36) * mm]});
            skLineSegment(sketch, "E707", {"start": v(-8.55, 7.36) * mm, "end": v(-8.6, 7.86) * mm});
            skLineSegment(sketch, "E708", {"start": v(-8.6, 7.86) * mm, "end": v(-8.58, 7.9) * mm});
            skLineSegment(sketch, "E709", {"start": v(-8.58, 7.9) * mm, "end": v(-8.56, 7.96) * mm});
            skLineSegment(sketch, "E710", {"start": v(-8.56, 7.96) * mm, "end": v(-8.16, 7.94) * mm});
            skLineSegment(sketch, "E711", {"start": v(-8.16, 7.94) * mm, "end": v(-7.76, 7.91) * mm});
            skLineSegment(sketch, "E712", {"start": v(-7.76, 7.91) * mm, "end": v(-7.5, 7.87) * mm});
            skFitSpline(sketch, "E713", {"points": [v(-7.5, 7.87) * mm, v(-7.37, 7.84) * mm, v(-7.14, 7.78) * mm, v(-7, 7.73) * mm]});
            skLineSegment(sketch, "E714", {"start": v(-7, 7.73) * mm, "end": v(-6.76, 7.65) * mm});
            skLineSegment(sketch, "E715", {"start": v(-6.76, 7.65) * mm, "end": v(-6.47, 7.5) * mm});
            skLineSegment(sketch, "E716", {"start": v(-6.47, 7.5) * mm, "end": v(-6.18, 7.34) * mm});
            skLineSegment(sketch, "E717", {"start": v(-6.18, 7.34) * mm, "end": v(-5.91, 7.12) * mm});
            skLineSegment(sketch, "E718", {"start": v(-5.91, 7.12) * mm, "end": v(-5.65, 6.91) * mm});
            skLineSegment(sketch, "E719", {"start": v(-5.65, 6.91) * mm, "end": v(-5.43, 6.68) * mm});
            skFitSpline(sketch, "E720", {"points": [v(-5.43, 6.68) * mm, v(-5.3, 6.56) * mm, v(-5.21, 6.44) * mm, v(-5.21, 6.43) * mm]});
            skFitSpline(sketch, "E721", {"points": [v(-5.21, 6.43) * mm, v(-5.21, 6.41) * mm, v(-7.04, 5.16) * mm, v(-7.6, 4.79) * mm]});
            skLineSegment(sketch, "E722", {"start": v(-7.6, 4.79) * mm, "end": v(-7.7, 4.72) * mm});
            skLineSegment(sketch, "E723", {"start": v(-7.7, 4.72) * mm, "end": v(-7.8, 4.87) * mm});
            skFitSpline(sketch, "E724", {"points": [v(-6.47, 5.66) * mm, v(-5.85, 6.08) * mm, v(-5.34, 6.44) * mm, v(-5.34, 6.45) * mm]});
            skFitSpline(sketch, "E725", {"points": [v(-5.34, 6.45) * mm, v(-5.34, 6.5) * mm, v(-5.89, 7) * mm, v(-6.1, 7.17) * mm]});
            skLineSegment(sketch, "E726", {"start": v(-6.1, 7.17) * mm, "end": v(-6.32, 7.33) * mm});
            skLineSegment(sketch, "E727", {"start": v(-6.32, 7.33) * mm, "end": v(-6.6, 7.47) * mm});
            skLineSegment(sketch, "E728", {"start": v(-6.6, 7.47) * mm, "end": v(-6.89, 7.61) * mm});
            skLineSegment(sketch, "E729", {"start": v(-6.89, 7.61) * mm, "end": v(-7.12, 7.68) * mm});
            skLineSegment(sketch, "E730", {"start": v(-7.12, 7.68) * mm, "end": v(-7.35, 7.75) * mm});
            skLineSegment(sketch, "E731", {"start": v(-7.35, 7.75) * mm, "end": v(-7.67, 7.8) * mm});
            skLineSegment(sketch, "E732", {"start": v(-7.67, 7.8) * mm, "end": v(-7.98, 7.85) * mm});
            skLineSegment(sketch, "E733", {"start": v(-7.98, 7.85) * mm, "end": v(-8.24, 7.85) * mm});
            skLineSegment(sketch, "E734", {"start": v(-8.24, 7.85) * mm, "end": v(-8.5, 7.85) * mm});
            skLineSegment(sketch, "E735", {"start": v(-8.5, 7.85) * mm, "end": v(-8.5, 7.76) * mm});
            skFitSpline(sketch, "E736", {"points": [v(-8.5, 7.76) * mm, v(-8.5, 7.7) * mm, v(-8.48, 7.47) * mm, v(-8.45, 7.24) * mm]});
            skFitSpline(sketch, "E737", {"points": [v(-8.45, 7.24) * mm, v(-8.32, 6.14) * mm, v(-8.16, 5.58) * mm, v(-7.83, 5.07) * mm]});
            skLineSegment(sketch, "E738", {"start": v(-7.83, 5.07) * mm, "end": v(-7.7, 4.86) * mm});
            skLineSegment(sketch, "E739", {"start": v(-7.7, 4.86) * mm, "end": v(-7.65, 4.88) * mm});
            skFitSpline(sketch, "E740", {"points": [v(-7.65, 4.88) * mm, v(-7.62, 4.89) * mm, v(-7.1, 5.24) * mm, v(-6.47, 5.66) * mm]});
            skLineSegment(sketch, "E741", {"start": v(-6.47, 5.66) * mm, "end": v(-6.47, 5.66) * mm});
            skFitSpline(sketch, "E742", {"points": [v(6.44, 5.56) * mm, v(5.78, 6.02) * mm, v(5.23, 6.4) * mm, v(5.22, 6.43) * mm]});
            skLineSegment(sketch, "E743", {"start": v(5.22, 6.43) * mm, "end": v(5.2, 6.46) * mm});
            skLineSegment(sketch, "E744", {"start": v(5.2, 6.46) * mm, "end": v(5.54, 6.78) * mm});
            skLineSegment(sketch, "E745", {"start": v(5.54, 6.78) * mm, "end": v(5.86, 7.1) * mm});
            skLineSegment(sketch, "E746", {"start": v(5.86, 7.1) * mm, "end": v(6.12, 7.28) * mm});
            skLineSegment(sketch, "E747", {"start": v(6.12, 7.28) * mm, "end": v(6.38, 7.46) * mm});
            skLineSegment(sketch, "E748", {"start": v(6.38, 7.46) * mm, "end": v(6.66, 7.59) * mm});
            skLineSegment(sketch, "E749", {"start": v(6.66, 7.59) * mm, "end": v(6.94, 7.72) * mm});
            skLineSegment(sketch, "E750", {"start": v(6.94, 7.72) * mm, "end": v(7.27, 7.8) * mm});
            skLineSegment(sketch, "E751", {"start": v(7.27, 7.8) * mm, "end": v(7.59, 7.9) * mm});
            skLineSegment(sketch, "E752", {"start": v(7.59, 7.9) * mm, "end": v(8.1, 7.9) * mm});
            skLineSegment(sketch, "E753", {"start": v(8.1, 7.9) * mm, "end": v(8.6, 7.93) * mm});
            skLineSegment(sketch, "E754", {"start": v(8.6, 7.93) * mm, "end": v(8.6, 7.88) * mm});
            skFitSpline(sketch, "E755", {"points": [v(8.6, 7.88) * mm, v(8.6, 7.85) * mm, v(8.57, 7.57) * mm, v(8.53, 7.25) * mm]});
            skFitSpline(sketch, "E756", {"points": [v(8.53, 7.25) * mm, v(8.46, 6.59) * mm, v(8.4, 6.26) * mm, v(8.28, 5.86) * mm]});
            skLineSegment(sketch, "E757", {"start": v(8.28, 5.86) * mm, "end": v(8.2, 5.58) * mm});
            skLineSegment(sketch, "E758", {"start": v(8.2, 5.58) * mm, "end": v(8.07, 5.31) * mm});
            skFitSpline(sketch, "E759", {"points": [v(8.07, 5.31) * mm, v(7.93, 5.04) * mm, v(7.72, 4.73) * mm, v(7.68, 4.73) * mm]});
            skFitSpline(sketch, "E760", {"points": [v(7.68, 4.73) * mm, v(7.67, 4.73) * mm, v(7.1, 5.1) * mm, v(6.44, 5.56) * mm]});
            skFitSpline(sketch, "E761", {"points": [v(7.85, 5.1) * mm, v(8.18, 5.63) * mm, v(8.32, 6.15) * mm, v(8.45, 7.27) * mm]});
            skFitSpline(sketch, "E762", {"points": [v(8.45, 7.27) * mm, v(8.48, 7.5) * mm, v(8.5, 7.73) * mm, v(8.5, 7.78) * mm]});
            skLineSegment(sketch, "E763", {"start": v(8.5, 7.78) * mm, "end": v(8.5, 7.85) * mm});
            skLineSegment(sketch, "E764", {"start": v(8.5, 7.85) * mm, "end": v(8.3, 7.85) * mm});
            skFitSpline(sketch, "E765", {"points": [v(8.3, 7.85) * mm, v(8.18, 7.85) * mm, v(7.95, 7.83) * mm, v(7.79, 7.81) * mm]});
            skLineSegment(sketch, "E766", {"start": v(7.79, 7.81) * mm, "end": v(7.49, 7.78) * mm});
            skLineSegment(sketch, "E767", {"start": v(7.49, 7.78) * mm, "end": v(7.2, 7.7) * mm});
            skLineSegment(sketch, "E768", {"start": v(7.2, 7.7) * mm, "end": v(6.92, 7.62) * mm});
            skLineSegment(sketch, "E769", {"start": v(6.92, 7.62) * mm, "end": v(6.69, 7.5) * mm});
            skFitSpline(sketch, "E770", {"points": [v(6.69, 7.5) * mm, v(6.56, 7.44) * mm, v(6.33, 7.32) * mm, v(6.2, 7.22) * mm]});
            skLineSegment(sketch, "E771", {"start": v(6.2, 7.22) * mm, "end": v(5.94, 7.05) * mm});
            skLineSegment(sketch, "E772", {"start": v(5.94, 7.05) * mm, "end": v(5.64, 6.76) * mm});
            skLineSegment(sketch, "E773", {"start": v(5.64, 6.76) * mm, "end": v(5.33, 6.46) * mm});
            skLineSegment(sketch, "E774", {"start": v(5.33, 6.46) * mm, "end": v(5.37, 6.42) * mm});
            skFitSpline(sketch, "E775", {"points": [v(5.37, 6.42) * mm, v(5.45, 6.34) * mm, v(7.62, 4.87) * mm, v(7.66, 4.86) * mm]});
            skLineSegment(sketch, "E776", {"start": v(7.66, 4.86) * mm, "end": v(7.7, 4.86) * mm});
            skLineSegment(sketch, "E777", {"start": v(7.7, 4.86) * mm, "end": v(7.85, 5.1) * mm});
            skLineSegment(sketch, "E778", {"start": v(7.85, 5.1) * mm, "end": v(7.85, 5.1) * mm});
            skFitSpline(sketch, "E779", {"points": [v(-0.5, 5.6) * mm, v(-0.58, 5.61) * mm, v(-0.71, 5.66) * mm, v(-0.8, 5.7) * mm]});
            skLineSegment(sketch, "E780", {"start": v(-0.8, 5.7) * mm, "end": v(-0.98, 5.79) * mm});
            skLineSegment(sketch, "E781", {"start": v(-0.98, 5.79) * mm, "end": v(-1.12, 5.93) * mm});
            skFitSpline(sketch, "E782", {"points": [v(-1.12, 5.93) * mm, v(-1.2, 6) * mm, v(-1.3, 6.13) * mm, v(-1.35, 6.2) * mm]});
            skLineSegment(sketch, "E783", {"start": v(-1.35, 6.2) * mm, "end": v(-1.42, 6.34) * mm});
            skLineSegment(sketch, "E784", {"start": v(-1.42, 6.34) * mm, "end": v(-1.48, 6.56) * mm});
            skLineSegment(sketch, "E785", {"start": v(-1.48, 6.56) * mm, "end": v(-1.53, 6.77) * mm});
            skLineSegment(sketch, "E786", {"start": v(-1.53, 6.77) * mm, "end": v(-1.52, 7) * mm});
            skLineSegment(sketch, "E787", {"start": v(-1.52, 7) * mm, "end": v(-1.5, 7.24) * mm});
            skLineSegment(sketch, "E788", {"start": v(-1.5, 7.24) * mm, "end": v(-1.43, 7.43) * mm});
            skLineSegment(sketch, "E789", {"start": v(-1.43, 7.43) * mm, "end": v(-1.36, 7.62) * mm});
            skLineSegment(sketch, "E790", {"start": v(-1.36, 7.62) * mm, "end": v(-1.23, 7.79) * mm});
            skLineSegment(sketch, "E791", {"start": v(-1.23, 7.79) * mm, "end": v(-1.1, 7.96) * mm});
            skLineSegment(sketch, "E792", {"start": v(-1.1, 7.96) * mm, "end": v(-0.93, 8.08) * mm});
            skLineSegment(sketch, "E793", {"start": v(-0.93, 8.08) * mm, "end": v(-0.76, 8.21) * mm});
            skLineSegment(sketch, "E794", {"start": v(-0.76, 8.21) * mm, "end": v(-0.57, 8.29) * mm});
            skLineSegment(sketch, "E795", {"start": v(-0.57, 8.29) * mm, "end": v(-0.38, 8.36) * mm});
            skLineSegment(sketch, "E796", {"start": v(-0.38, 8.36) * mm, "end": v(0, 8.36) * mm});
            skLineSegment(sketch, "E797", {"start": v(0, 8.36) * mm, "end": v(0.38, 8.36) * mm});
            skLineSegment(sketch, "E798", {"start": v(0.38, 8.36) * mm, "end": v(0.57, 8.27) * mm});
            skLineSegment(sketch, "E799", {"start": v(0.57, 8.27) * mm, "end": v(0.76, 8.18) * mm});
            skLineSegment(sketch, "E800", {"start": v(0.76, 8.18) * mm, "end": v(0.9, 8.04) * mm});
            skLineSegment(sketch, "E801", {"start": v(0.9, 8.04) * mm, "end": v(1.03, 7.89) * mm});
            skLineSegment(sketch, "E802", {"start": v(1.03, 7.89) * mm, "end": v(1.13, 7.7) * mm});
            skLineSegment(sketch, "E803", {"start": v(1.13, 7.7) * mm, "end": v(1.23, 7.5) * mm});
            skLineSegment(sketch, "E804", {"start": v(1.23, 7.5) * mm, "end": v(1.28, 7.22) * mm});
            skLineSegment(sketch, "E805", {"start": v(1.28, 7.22) * mm, "end": v(1.34, 6.95) * mm});
            skLineSegment(sketch, "E806", {"start": v(1.34, 6.95) * mm, "end": v(1.3, 6.75) * mm});
            skLineSegment(sketch, "E807", {"start": v(1.3, 6.75) * mm, "end": v(1.26, 6.55) * mm});
            skLineSegment(sketch, "E808", {"start": v(1.26, 6.55) * mm, "end": v(1.17, 6.34) * mm});
            skLineSegment(sketch, "E809", {"start": v(1.17, 6.34) * mm, "end": v(1.07, 6.13) * mm});
            skLineSegment(sketch, "E810", {"start": v(1.07, 6.13) * mm, "end": v(0.91, 5.96) * mm});
            skLineSegment(sketch, "E811", {"start": v(0.91, 5.96) * mm, "end": v(0.75, 5.8) * mm});
            skLineSegment(sketch, "E812", {"start": v(0.75, 5.8) * mm, "end": v(0.54, 5.68) * mm});
            skLineSegment(sketch, "E813", {"start": v(0.54, 5.68) * mm, "end": v(0.32, 5.58) * mm});
            skLineSegment(sketch, "E814", {"start": v(0.32, 5.58) * mm, "end": v(-0.03, 5.57) * mm});
            skLineSegment(sketch, "E815", {"start": v(-0.03, 5.57) * mm, "end": v(-0.38, 5.56) * mm});
            skLineSegment(sketch, "E816", {"start": v(-0.38, 5.56) * mm, "end": v(-0.5, 5.6) * mm});
            skLineSegment(sketch, "E817", {"start": v(-0.5, 5.6) * mm, "end": v(-0.5, 5.6) * mm});
            skLineSegment(sketch, "E818", {"start": v(0.46, 5.74) * mm, "end": v(0.66, 5.83) * mm});
            skLineSegment(sketch, "E819", {"start": v(0.66, 5.83) * mm, "end": v(0.82, 6) * mm});
            skLineSegment(sketch, "E820", {"start": v(0.82, 6) * mm, "end": v(1, 6.17) * mm});
            skLineSegment(sketch, "E821", {"start": v(1, 6.17) * mm, "end": v(1.08, 6.34) * mm});
            skFitSpline(sketch, "E822", {"points": [v(1.08, 6.34) * mm, v(1.18, 6.54) * mm, v(1.23, 6.75) * mm, v(1.23, 6.96) * mm]});
            skLineSegment(sketch, "E823", {"start": v(1.23, 6.96) * mm, "end": v(1.23, 7.1) * mm});
            skLineSegment(sketch, "E824", {"start": v(1.23, 7.1) * mm, "end": v(1.18, 7.3) * mm});
            skFitSpline(sketch, "E825", {"points": [v(1.18, 7.3) * mm, v(1.15, 7.4) * mm, v(1.09, 7.57) * mm, v(1.04, 7.66) * mm]});
            skLineSegment(sketch, "E826", {"start": v(1.04, 7.66) * mm, "end": v(0.96, 7.83) * mm});
            skLineSegment(sketch, "E827", {"start": v(0.96, 7.83) * mm, "end": v(0.82, 7.98) * mm});
            skLineSegment(sketch, "E828", {"start": v(0.82, 7.98) * mm, "end": v(0.68, 8.12) * mm});
            skLineSegment(sketch, "E829", {"start": v(0.68, 8.12) * mm, "end": v(0.56, 8.18) * mm});
            skLineSegment(sketch, "E830", {"start": v(0.56, 8.18) * mm, "end": v(0.44, 8.25) * mm});
            skLineSegment(sketch, "E831", {"start": v(0.44, 8.25) * mm, "end": v(0.23, 8.28) * mm});
            skLineSegment(sketch, "E832", {"start": v(0.23, 8.28) * mm, "end": v(0.02, 8.31) * mm});
            skLineSegment(sketch, "E833", {"start": v(0.02, 8.31) * mm, "end": v(-0.21, 8.28) * mm});
            skLineSegment(sketch, "E834", {"start": v(-0.21, 8.28) * mm, "end": v(-0.45, 8.25) * mm});
            skLineSegment(sketch, "E835", {"start": v(-0.45, 8.25) * mm, "end": v(-0.65, 8.15) * mm});
            skLineSegment(sketch, "E836", {"start": v(-0.65, 8.15) * mm, "end": v(-0.86, 8.05) * mm});
            skLineSegment(sketch, "E837", {"start": v(-0.86, 8.05) * mm, "end": v(-1.02, 7.9) * mm});
            skLineSegment(sketch, "E838", {"start": v(-1.02, 7.9) * mm, "end": v(-1.18, 7.73) * mm});
            skLineSegment(sketch, "E839", {"start": v(-1.18, 7.73) * mm, "end": v(-1.29, 7.52) * mm});
            skLineSegment(sketch, "E840", {"start": v(-1.29, 7.52) * mm, "end": v(-1.4, 7.3) * mm});
            skLineSegment(sketch, "E841", {"start": v(-1.4, 7.3) * mm, "end": v(-1.42, 7.1) * mm});
            skLineSegment(sketch, "E842", {"start": v(-1.42, 7.1) * mm, "end": v(-1.45, 6.9) * mm});
            skLineSegment(sketch, "E843", {"start": v(-1.45, 6.9) * mm, "end": v(-1.42, 6.7) * mm});
            skLineSegment(sketch, "E844", {"start": v(-1.42, 6.7) * mm, "end": v(-1.4, 6.5) * mm});
            skLineSegment(sketch, "E845", {"start": v(-1.4, 6.5) * mm, "end": v(-1.31, 6.34) * mm});
            skLineSegment(sketch, "E846", {"start": v(-1.31, 6.34) * mm, "end": v(-1.23, 6.16) * mm});
            skLineSegment(sketch, "E847", {"start": v(-1.23, 6.16) * mm, "end": v(-1.09, 6.01) * mm});
            skLineSegment(sketch, "E848", {"start": v(-1.09, 6.01) * mm, "end": v(-0.94, 5.87) * mm});
            skLineSegment(sketch, "E849", {"start": v(-0.94, 5.87) * mm, "end": v(-0.75, 5.78) * mm});
            skLineSegment(sketch, "E850", {"start": v(-0.75, 5.78) * mm, "end": v(-0.57, 5.7) * mm});
            skLineSegment(sketch, "E851", {"start": v(-0.57, 5.7) * mm, "end": v(-0.4, 5.66) * mm});
            skLineSegment(sketch, "E852", {"start": v(-0.4, 5.66) * mm, "end": v(-0.21, 5.63) * mm});
            skLineSegment(sketch, "E853", {"start": v(-0.21, 5.63) * mm, "end": v(0.03, 5.64) * mm});
            skLineSegment(sketch, "E854", {"start": v(0.03, 5.64) * mm, "end": v(0.27, 5.66) * mm});
            skLineSegment(sketch, "E855", {"start": v(0.27, 5.66) * mm, "end": v(0.46, 5.74) * mm});
            skLineSegment(sketch, "E856.0", {"start": v(-4.61, 1.4) * mm, "end": v(-4.87, 1.3) * mm});
            skLineSegment(sketch, "E856.1", {"start": v(-4.35, 1.48) * mm, "end": v(-4.61, 1.4) * mm});
            skLineSegment(sketch, "E856.2", {"start": v(-4.1, 1.52) * mm, "end": v(-4.35, 1.48) * mm});
            skLineSegment(sketch, "E856.3", {"start": v(-3.84, 1.55) * mm, "end": v(-4.1, 1.52) * mm});
            skLineSegment(sketch, "E856.4", {"start": v(-3.61, 1.52) * mm, "end": v(-3.84, 1.55) * mm});
            skLineSegment(sketch, "E856.5", {"start": v(-4.87, 1.3) * mm, "end": v(-5.2, 1.14) * mm});
            skLineSegment(sketch, "E856.6", {"start": v(-3.39, 1.48) * mm, "end": v(-3.61, 1.52) * mm});
            skLineSegment(sketch, "E856.7", {"start": v(-3.16, 1.39) * mm, "end": v(-3.39, 1.48) * mm});
            skLineSegment(sketch, "E856.8", {"start": v(-2.9, 1.29) * mm, "end": v(-3.16, 1.39) * mm});
            skLineSegment(sketch, "E856.9", {"start": v(-2.2, 0.23) * mm, "end": v(-2.9, 1.29) * mm});
            skLineSegment(sketch, "E856.10", {"start": v(-5.56, -0.76) * mm, "end": v(-5.3, -0.93) * mm});
            skLineSegment(sketch, "E856.11", {"start": v(-5.84, -0.48) * mm, "end": v(-5.56, -0.76) * mm});
            skFitSpline(sketch, "E856.12", {"points": [v(-6.45, 0.3) * mm, v(-6.45, 0.28) * mm, v(-6.44, 0.25) * mm, v(-6.42, 0.21) * mm, v(-6.4, 0.18) * mm, v(-6.37, 0.13) * mm, v(-6.32, 0.06) * mm, v(-6.23, -0.04) * mm, v(-6.14, -0.15) * mm, v(-6, -0.3) * mm, v(-5.9, -0.42) * mm, v(-5.84, -0.48) * mm]});
            skFitSpline(sketch, "E856.13", {"points": [v(-5.2, 1.14) * mm, v(-5.25, 1.11) * mm, v(-5.36, 1.05) * mm, v(-5.55, 0.94) * mm, v(-5.75, 0.82) * mm, v(-5.92, 0.72) * mm, v(-6.04, 0.64) * mm, v(-6.12, 0.6) * mm, v(-6.2, 0.54) * mm, v(-6.27, 0.5) * mm, v(-6.32, 0.46) * mm, v(-6.35, 0.44) * mm, v(-6.37, 0.42) * mm, v(-6.39, 0.4) * mm, v(-6.4, 0.4) * mm, v(-6.41, 0.39) * mm, v(-6.42, 0.38) * mm, v(-6.44, 0.36) * mm, v(-6.45, 0.33) * mm, v(-6.45, 0.3) * mm]});
            skFitSpline(sketch, "E856.14", {"points": [v(-5.3, -0.93) * mm, v(-5.2, -1) * mm, v(-5, -1.12) * mm, v(-4.66, -1.29) * mm, v(-4.41, -1.39) * mm, v(-4.25, -1.44) * mm, v(-4.18, -1.45) * mm, v(-4.15, -1.45) * mm]});
            skFitSpline(sketch, "E856.15", {"points": [v(-4.15, -1.45) * mm, v(-4.14, -1.45) * mm, v(-4.14, -1.45) * mm, v(-4.11, -1.45) * mm, v(-4.08, -1.45) * mm, v(-4.02, -1.45) * mm, v(-3.93, -1.44) * mm, v(-3.78, -1.43) * mm, v(-3.64, -1.41) * mm, v(-3.57, -1.4) * mm]});
            skFitSpline(sketch, "E856.16", {"points": [v(-3.57, -1.4) * mm, v(-2.73, -1.32) * mm, v(-2.24, -1.24) * mm, v(-1.64, -1.07) * mm]});
            skLineSegment(sketch, "E856.17", {"start": v(-1.64, -1.07) * mm, "end": v(-1.44, -1.01) * mm});
            skLineSegment(sketch, "E856.18", {"start": v(-1.44, -1.01) * mm, "end": v(-1.5, -0.86) * mm});
            skFitSpline(sketch, "E856.19", {"points": [v(-1.5, -0.86) * mm, v(-1.5, -0.86) * mm, v(-1.5, -0.85) * mm, v(-1.5, -0.84) * mm, v(-1.51, -0.84) * mm, v(-1.52, -0.83) * mm, v(-1.53, -0.81) * mm, v(-1.54, -0.79) * mm, v(-1.57, -0.75) * mm, v(-1.6, -0.7) * mm, v(-1.65, -0.63) * mm, v(-1.72, -0.52) * mm, v(-1.82, -0.36) * mm, v(-1.98, -0.12) * mm, v(-2.11, 0.09) * mm, v(-2.2, 0.23) * mm]});
            skSolve(sketch);
        }
        {
            var Q0;
            Q0=makeQuery(id+"F0.imprint","IMPRINT",FACE,{"disambiguationData":[TD([[makeQuery(id+"F0.imprint","IMPRINT",EDGE,{"derivedFrom":sQuery(id+"F0.wireOp",EDGE,"E0")}),-1.0]])]});
            var Q1;
            Q1=makeQuery(id+"F0.imprint","IMPRINT",FACE,{"disambiguationData":[TD([[makeQuery(id+"F0.imprint","IMPRINT",EDGE,{"derivedFrom":sQuery(id+"F0.wireOp",EDGE,"E701")}),-1.0]])]});
            var Q2;
            Q2=makeQuery(id+"F0.imprint","IMPRINT",FACE,{"disambiguationData":[TD([[makeQuery(id+"F0.imprint","IMPRINT",EDGE,{"derivedFrom":sQuery(id+"F0.wireOp",EDGE,"E779")}),-1.0]])]});
            var Q3;
            Q3=makeQuery(id+"F0.imprint","IMPRINT",FACE,{"disambiguationData":[TD([[makeQuery(id+"F0.imprint","IMPRINT",EDGE,{"derivedFrom":sQuery(id+"F0.wireOp",EDGE,"E566")}),-1.0]])]});
            var Q4;
            Q4=makeQuery(id+"F0.imprint","IMPRINT",FACE,{"disambiguationData":[TD([[makeQuery(id+"F0.imprint","IMPRINT",EDGE,{"derivedFrom":sQuery(id+"F0.wireOp",EDGE,"E504")}),-1.0]])]});
            var Q5;
            Q5=makeQuery(id+"F0.imprint","IMPRINT",FACE,{"disambiguationData":[TD([[makeQuery(id+"F0.imprint","IMPRINT",EDGE,{"derivedFrom":sQuery(id+"F0.wireOp",EDGE,"E690")}),-1.0]])]});
            var Q6;
            Q6=makeQuery(id+"F0.imprint","IMPRINT",FACE,{"disambiguationData":[TD([[makeQuery(id+"F0.imprint","IMPRINT",EDGE,{"derivedFrom":sQuery(id+"F0.wireOp",EDGE,"E627")}),-1.0]])]});
            var Q7;
            Q7=makeQuery(id+"F0.imprint","IMPRINT",FACE,{"disambiguationData":[TD([[makeQuery(id+"F0.imprint","IMPRINT",EDGE,{"derivedFrom":sQuery(id+"F0.wireOp",EDGE,"E742")}),-1.0]])]});
            var Q8;
            Q8=makeQuery(id+"F0.imprint","IMPRINT",FACE,{"disambiguationData":[TD([[makeQuery(id+"F0.imprint","IMPRINT",EDGE,{"derivedFrom":sQuery(id+"F0.wireOp",EDGE,"E397")}),-1.0]])]});
            var Q9;
            Q9=makeQuery(id+"F0.imprint","IMPRINT",FACE,{"disambiguationData":[TD([[makeQuery(id+"F0.imprint","IMPRINT",EDGE,{"derivedFrom":sQuery(id+"F0.wireOp",EDGE,"E432")}),-1.0]])]});
            var Q10;
            Q10=makeQuery(id+"F0.imprint","IMPRINT",FACE,{"disambiguationData":[TD([[makeQuery(id+"F0.imprint","IMPRINT",EDGE,{"derivedFrom":sQuery(id+"F0.wireOp",EDGE,"E467")}),-1.0]])]});
            var Q11;
            Q11=makeQuery(id+"F0.imprint","IMPRINT",FACE,{"disambiguationData":[TD([[makeQuery(id+"F0.imprint","IMPRINT",EDGE,{"derivedFrom":sQuery(id+"F0.wireOp",EDGE,"E300")}),-1.0]])]});
            var Q12;
            Q12=makeQuery(id+"F0.imprint","IMPRINT",FACE,{"disambiguationData":[TD([[makeQuery(id+"F0.imprint","IMPRINT",EDGE,{"derivedFrom":sQuery(id+"F0.wireOp",EDGE,"E413")}),-1.0]])]});
            var Q13;
            Q13=makeQuery(id+"F0.imprint","IMPRINT",FACE,{"disambiguationData":[TD([[makeQuery(id+"F0.imprint","IMPRINT",EDGE,{"derivedFrom":sQuery(id+"F0.wireOp",EDGE,"E451")}),-1.0]])]});
            var Q14;
            Q14=makeQuery(id+"F0.imprint","IMPRINT",FACE,{"disambiguationData":[TD([[makeQuery(id+"F0.imprint","IMPRINT",EDGE,{"derivedFrom":sQuery(id+"F0.wireOp",EDGE,"E382")}),-1.0]])]});
            extrude(context, id + "F1", {"entities" : qUnion([Q0, Q1, Q2, Q3, Q4, Q5, Q6, Q7, Q8, Q9, Q10, Q11, Q12, Q13, Q14]), "depth" : 1 * mm});
        }
        {
            var Q0;
            Q0=makeQuery(id+"F0.imprint","IMPRINT",FACE,{"disambiguationData":[TD([[makeQuery(id+"F0.imprint","IMPRINT",EDGE,{"derivedFrom":sQuery(id+"F0.wireOp",EDGE,"E156")}),1.0]])]});
            var Q1;
            Q1=makeQuery(id+"F0.imprint","IMPRINT",FACE,{"disambiguationData":[TD([[makeQuery(id+"F0.imprint","IMPRINT",EDGE,{"derivedFrom":sQuery(id+"F0.wireOp",EDGE,"E724")}),1.0]])]});
            var Q2;
            Q2=makeQuery(id+"F0.imprint","IMPRINT",FACE,{"disambiguationData":[TD([[makeQuery(id+"F0.imprint","IMPRINT",EDGE,{"derivedFrom":sQuery(id+"F0.wireOp",EDGE,"E818")}),1.0]])]});
            var Q3;
            Q3=makeQuery(id+"F0.imprint","IMPRINT",FACE,{"disambiguationData":[TD([[makeQuery(id+"F0.imprint","IMPRINT",EDGE,{"derivedFrom":sQuery(id+"F0.wireOp",EDGE,"E761")}),1.0]])]});
            var Q4;
            Q4=makeQuery(id+"F0.imprint","IMPRINT",FACE,{"disambiguationData":[TD([[makeQuery(id+"F0.imprint","IMPRINT",EDGE,{"derivedFrom":sQuery(id+"F0.wireOp",EDGE,"E484")}),1.0]])]});
            var Q5;
            Q5=makeQuery(id+"F0.imprint","IMPRINT",FACE,{"disambiguationData":[TD([[makeQuery(id+"F0.imprint","IMPRINT",EDGE,{"derivedFrom":sQuery(id+"F0.wireOp",EDGE,"E536")}),1.0]])]});
            var Q6;
            Q6=makeQuery(id+"F0.imprint","IMPRINT",FACE,{"disambiguationData":[TD([[makeQuery(id+"F0.imprint","IMPRINT",EDGE,{"derivedFrom":sQuery(id+"F0.wireOp",EDGE,"E572")}),-1.0]])]});
            var Q7;
            Q7=makeQuery(id+"F0.imprint","IMPRINT",FACE,{"disambiguationData":[TD([[makeQuery(id+"F0.imprint","IMPRINT",EDGE,{"derivedFrom":sQuery(id+"F0.wireOp",EDGE,"E659")}),1.0]])]});
            var Q8;
            Q8=makeQuery(id+"F0.imprint","IMPRINT",FACE,{"disambiguationData":[TD([[makeQuery(id+"F0.imprint","IMPRINT",EDGE,{"derivedFrom":sQuery(id+"F0.wireOp",EDGE,"E365")}),1.0]])]});
            extrude(context, id + "F2", {"entities" : qUnion([Q0, Q1, Q2, Q3, Q4, Q5, Q6, Q7, Q8]), "operationType" : NewBodyOperationType.ADD, "depth" : 0.8 * mm});
        }
    });
